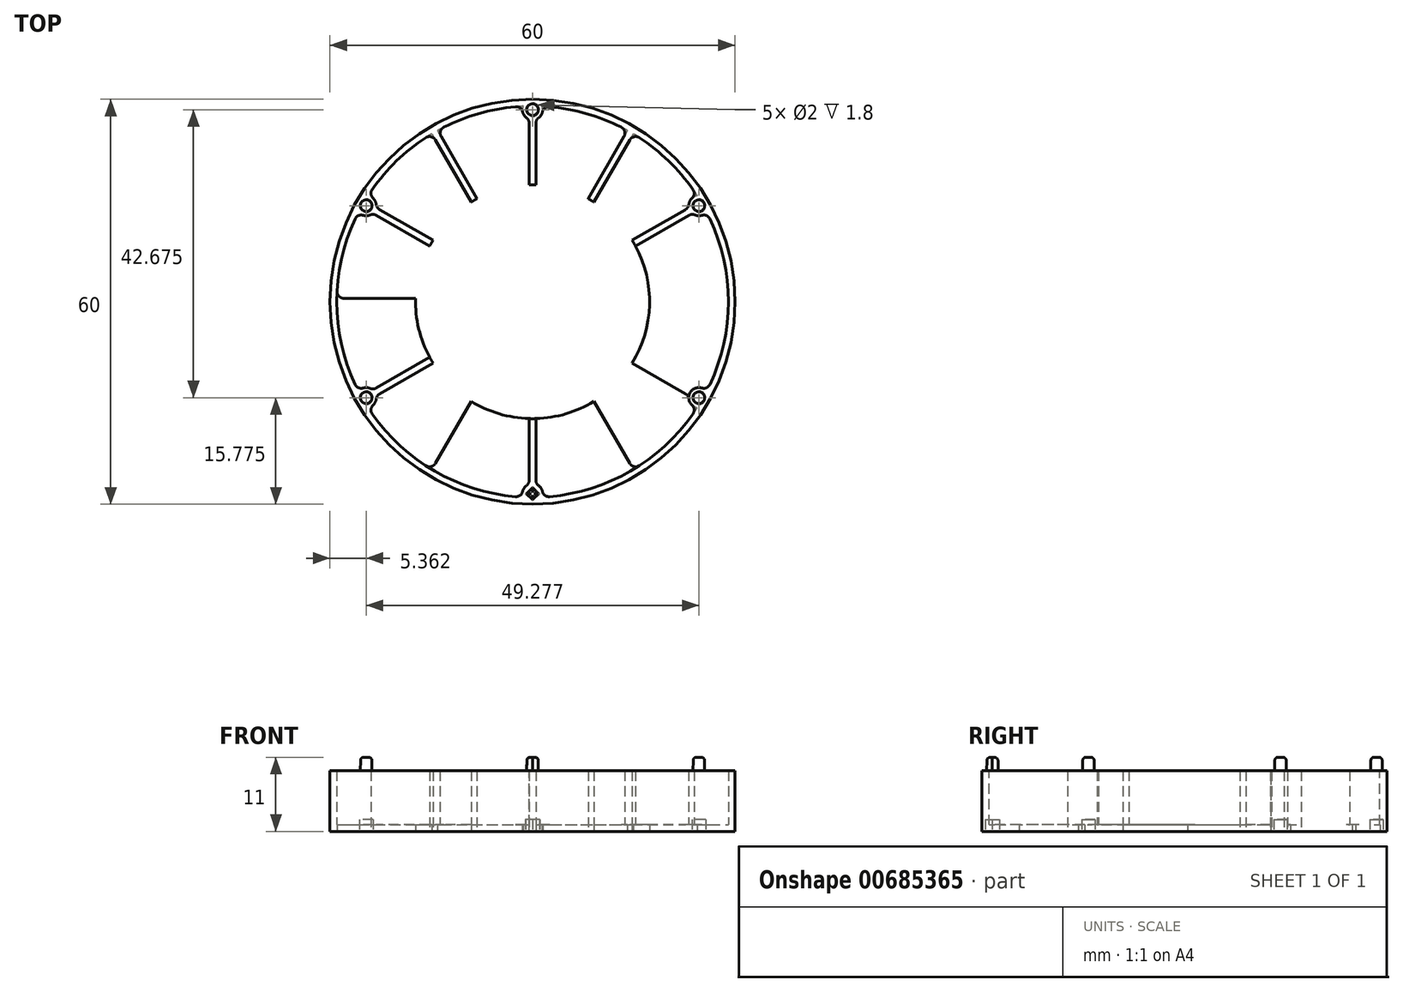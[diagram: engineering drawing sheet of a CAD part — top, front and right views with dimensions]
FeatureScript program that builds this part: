
annotation { "Feature Type Name" : "Feature", "Feature Type Description" : "" }
export const myFeature = defineFeature(function(context is Context, id is Id, definition is map)
    precondition{}
    {
        {
            var Q0;
            Q0=qCreatedBy(makeId("Top.planeOp"),FACE);
            var sketch = newSketch(context, id + "F0", { "sketchPlane" : qUnion([Q0])});
            skCircle(sketch, "E0", {"center": v(0, 0) * mm, "radius": 30 * mm});
            skCircle(sketch, "E1.0", {"center": v(0, 0) * mm, "radius": 29 * mm});
            skLineSegment(sketch, "E2.bottom", {"start": v(14.56, 26.23) * mm, "end": v(15.43, 25.73) * mm});
            skLineSegment(sketch, "E2.top", {"start": v(-15.43, -25.73) * mm, "end": v(-14.56, -26.23) * mm});
            skLineSegment(sketch, "E2.left", {"start": v(14.56, 26.23) * mm, "end": v(-15.43, -25.73) * mm});
            skLineSegment(sketch, "E2.right", {"start": v(15.43, 25.73) * mm, "end": v(-14.56, -26.23) * mm});
            skLineSegment(sketch, "E3.bottom", {"start": v(25.73, 15.43) * mm, "end": v(26.23, 14.56) * mm});
            skLineSegment(sketch, "E3.top", {"start": v(-26.23, -14.56) * mm, "end": v(-25.73, -15.43) * mm});
            skLineSegment(sketch, "E3.left", {"start": v(25.73, 15.43) * mm, "end": v(-26.23, -14.56) * mm});
            skLineSegment(sketch, "E3.right", {"start": v(26.23, 14.56) * mm, "end": v(-25.73, -15.43) * mm});
            skLineSegment(sketch, "E4", {"start": v(-38.35, 0) * mm, "end": v(39.17, 0) * mm, "construction": true});
            skLineSegment(sketch, "E5", {"start": v(0, 42.5) * mm, "end": v(0, -42.47) * mm, "construction": true});
            skLineSegment(sketch, "E6.bottom", {"start": v(-30, 0.5) * mm, "end": v(30, 0.5) * mm});
            skLineSegment(sketch, "E6.top", {"start": v(-30, -0.5) * mm, "end": v(30, -0.5) * mm});
            skLineSegment(sketch, "E6.left", {"start": v(-30, 0.5) * mm, "end": v(-30, -0.5) * mm});
            skLineSegment(sketch, "E6.right", {"start": v(30, 0.5) * mm, "end": v(30, -0.5) * mm});
            skLineSegment(sketch, "E7.bottom", {"start": v(-25.73, 15.43) * mm, "end": v(26.23, -14.56) * mm});
            skLineSegment(sketch, "E7.top", {"start": v(-26.23, 14.56) * mm, "end": v(25.73, -15.43) * mm});
            skLineSegment(sketch, "E7.left", {"start": v(-25.73, 15.43) * mm, "end": v(-26.23, 14.56) * mm});
            skLineSegment(sketch, "E7.right", {"start": v(26.23, -14.56) * mm, "end": v(25.73, -15.43) * mm});
            skLineSegment(sketch, "E8.bottom", {"start": v(-0.5, 30) * mm, "end": v(0.5, 30) * mm});
            skLineSegment(sketch, "E8.top", {"start": v(-0.5, -30) * mm, "end": v(0.5, -30) * mm});
            skLineSegment(sketch, "E8.left", {"start": v(-0.5, 30) * mm, "end": v(-0.5, -30) * mm});
            skLineSegment(sketch, "E8.right", {"start": v(0.5, 30) * mm, "end": v(0.5, -30) * mm});
            skLineSegment(sketch, "E9.bottom", {"start": v(-15.43, 25.73) * mm, "end": v(-14.56, 26.23) * mm});
            skLineSegment(sketch, "E9.top", {"start": v(14.56, -26.23) * mm, "end": v(15.43, -25.73) * mm});
            skLineSegment(sketch, "E9.left", {"start": v(-15.43, 25.73) * mm, "end": v(14.56, -26.23) * mm});
            skLineSegment(sketch, "E9.right", {"start": v(-14.56, 26.23) * mm, "end": v(15.43, -25.73) * mm});
            skCircle(sketch, "E10", {"center": v(0, 0) * mm, "radius": 17.33 * mm});
            skSolve(sketch);
        }
        {
            var Q0;
            Q0=qCreatedBy(makeId("Top.planeOp"),FACE);
            var sketch = newSketch(context, id + "F1", { "sketchPlane" : qUnion([Q0])});
            skCircle(sketch, "E11", {"center": v(0, 0) * mm, "radius": 30 * mm});
            skCircle(sketch, "E12", {"center": v(0, 0) * mm, "radius": 29 * mm});
            skSolve(sketch);
        }
        {
            var Q0;
            Q0=makeQuery(id+"F1.imprint","IMPRINT",FACE,{"disambiguationData":[TD([[makeQuery(id+"F1.imprint","IMPRINT",EDGE,{"derivedFrom":sQuery(id+"F1.wireOp",EDGE,"E11")}),1.0]])]});
            extrude(context, id + "F2", {"entities" : qUnion([Q0]), "depth" : 9 * mm, "offsetDistance" : 25 * mm});
        }
        {
            var Q0;
            {var subQ0=sQuery(id+"F0.wireOp",EDGE,"E7.bottom");var subQ1=sQuery(id+"F0.wireOp",EDGE,"E1.0");var subQ2=makeQuery(id+"F0.imprint","INTERSECT",VERTEX,{"disambiguationData":[OD(0.0)],"derivedFrom":[subQ1,subQ0]});Q0=makeQuery(id+"F0.imprint","IMPRINT",FACE,{"disambiguationData":[TD([[makeQuery(id+"F0.imprint","IMPRINT",EDGE,{"disambiguationData":[TD([[subQ2,-1.0]])],"derivedFrom":subQ1}),1.0]])]});}
            var Q1;
            {var subQ0=sQuery(id+"F0.wireOp",EDGE,"E2.right");var subQ1=sQuery(id+"F0.wireOp",EDGE,"E1.0");var subQ2=makeQuery(id+"F0.imprint","INTERSECT",VERTEX,{"disambiguationData":[OD(0.0)],"derivedFrom":[subQ1,subQ0]});Q1=makeQuery(id+"F0.imprint","IMPRINT",FACE,{"disambiguationData":[TD([[makeQuery(id+"F0.imprint","IMPRINT",EDGE,{"disambiguationData":[TD([[subQ2,-1.0]])],"derivedFrom":subQ1}),1.0]])]});}
            var Q2;
            {var subQ0=sQuery(id+"F0.wireOp",EDGE,"E8.left");var subQ1=sQuery(id+"F0.wireOp",EDGE,"E1.0");var subQ2=makeQuery(id+"F0.imprint","INTERSECT",VERTEX,{"disambiguationData":[OD(1.0)],"derivedFrom":[subQ1,subQ0]});Q2=makeQuery(id+"F0.imprint","IMPRINT",FACE,{"disambiguationData":[TD([[makeQuery(id+"F0.imprint","IMPRINT",EDGE,{"disambiguationData":[TD([[subQ2,-1.0]])],"derivedFrom":subQ1}),1.0]])]});}
            var Q3;
            {var subQ0=sQuery(id+"F0.wireOp",EDGE,"E3.left");var subQ1=sQuery(id+"F0.wireOp",EDGE,"E1.0");var subQ2=makeQuery(id+"F0.imprint","INTERSECT",VERTEX,{"disambiguationData":[OD(1.0)],"derivedFrom":[subQ1,subQ0]});Q3=makeQuery(id+"F0.imprint","IMPRINT",FACE,{"disambiguationData":[TD([[makeQuery(id+"F0.imprint","IMPRINT",EDGE,{"disambiguationData":[TD([[subQ2,-1.0]])],"derivedFrom":subQ1}),1.0]])]});}
            var Q4;
            {var subQ0=sQuery(id+"F0.wireOp",EDGE,"E9.right");var subQ1=sQuery(id+"F0.wireOp",EDGE,"E1.0");var subQ2=makeQuery(id+"F0.imprint","INTERSECT",VERTEX,{"disambiguationData":[OD(0.0)],"derivedFrom":[subQ1,subQ0]});Q4=makeQuery(id+"F0.imprint","IMPRINT",FACE,{"disambiguationData":[TD([[makeQuery(id+"F0.imprint","IMPRINT",EDGE,{"disambiguationData":[TD([[subQ2,-1.0]])],"derivedFrom":subQ1}),1.0]])]});}
            var Q5;
            {var subQ0=sQuery(id+"F0.wireOp",EDGE,"E8.right");var subQ1=sQuery(id+"F0.wireOp",EDGE,"E1.0");var subQ2=makeQuery(id+"F0.imprint","INTERSECT",VERTEX,{"disambiguationData":[OD(0.0)],"derivedFrom":[subQ1,subQ0]});Q5=makeQuery(id+"F0.imprint","IMPRINT",FACE,{"disambiguationData":[TD([[makeQuery(id+"F0.imprint","IMPRINT",EDGE,{"disambiguationData":[TD([[subQ2,-1.0]])],"derivedFrom":subQ1}),1.0]])]});}
            var Q6;
            {var subQ0=sQuery(id+"F0.wireOp",EDGE,"E3.right");var subQ1=sQuery(id+"F0.wireOp",EDGE,"E1.0");var subQ2=makeQuery(id+"F0.imprint","INTERSECT",VERTEX,{"disambiguationData":[OD(0.0)],"derivedFrom":[subQ1,subQ0]});Q6=makeQuery(id+"F0.imprint","IMPRINT",FACE,{"disambiguationData":[TD([[makeQuery(id+"F0.imprint","IMPRINT",EDGE,{"disambiguationData":[TD([[subQ2,-1.0]])],"derivedFrom":subQ1}),1.0]])]});}
            extrude(context, id + "F3", {"entities" : qUnion([Q0, Q1, Q2, Q3, Q4, Q5, Q6]), "operationType" : NewBodyOperationType.ADD, "depth" : 9 * mm, "offsetDistance" : 25 * mm});
        }
        {
            var Q0;
            Q0=makeQuery(id+"F1.imprint","IMPRINT",FACE,{"disambiguationData":[TD([[makeQuery(id+"F1.imprint","IMPRINT",EDGE,{"derivedFrom":sQuery(id+"F1.wireOp",EDGE,"E11")}),1.0]])]});
            var Q1;
            Q1=makeQuery(id+"F1.imprint","IMPRINT",FACE,{"disambiguationData":[TD([[makeQuery(id+"F1.imprint","IMPRINT",EDGE,{"derivedFrom":sQuery(id+"F1.wireOp",EDGE,"E12")}),1.0]])]});
            extrude(context, id + "F4", {"entities" : qUnion([Q0, Q1]), "operationType" : NewBodyOperationType.ADD, "depth" : 1 * mm, "offsetDistance" : 25 * mm});
        }
        {
            var Q0;
            {var subQ0=sQuery(id+"F0.wireOp",EDGE,"E9.right");var subQ1=sQuery(id+"F0.wireOp",EDGE,"E1.0");var subQ2=makeQuery(id+"F0.imprint","INTERSECT",VERTEX,{"disambiguationData":[OD(1.0)],"derivedFrom":[subQ1,subQ0]});Q0=makeQuery(id+"F0.imprint","IMPRINT",FACE,{"disambiguationData":[TD([[makeQuery(id+"F0.imprint","IMPRINT",EDGE,{"disambiguationData":[TD([[subQ2,-1.0]])],"derivedFrom":subQ1}),1.0]])]});}
            var Q1;
            {var subQ0=sQuery(id+"F0.wireOp",EDGE,"E3.left");var subQ1=sQuery(id+"F0.wireOp",EDGE,"E1.0");var subQ2=makeQuery(id+"F0.imprint","INTERSECT",VERTEX,{"disambiguationData":[OD(0.0)],"derivedFrom":[subQ1,subQ0]});Q1=makeQuery(id+"F0.imprint","IMPRINT",FACE,{"disambiguationData":[TD([[makeQuery(id+"F0.imprint","IMPRINT",EDGE,{"disambiguationData":[TD([[subQ2,-1.0]])],"derivedFrom":subQ1}),1.0]])]});}
            var Q2;
            {var subQ0=sQuery(id+"F0.wireOp",EDGE,"E2.left");var subQ1=sQuery(id+"F0.wireOp",EDGE,"E1.0");var subQ2=makeQuery(id+"F0.imprint","INTERSECT",VERTEX,{"disambiguationData":[OD(0.0)],"derivedFrom":[subQ1,subQ0]});Q2=makeQuery(id+"F0.imprint","IMPRINT",FACE,{"disambiguationData":[TD([[makeQuery(id+"F0.imprint","IMPRINT",EDGE,{"disambiguationData":[TD([[subQ2,-1.0]])],"derivedFrom":subQ1}),1.0]])]});}
            var Q3;
            {var subQ0=sQuery(id+"F0.wireOp",EDGE,"E8.left");var subQ1=sQuery(id+"F0.wireOp",EDGE,"E1.0");var subQ2=makeQuery(id+"F0.imprint","INTERSECT",VERTEX,{"disambiguationData":[OD(0.0)],"derivedFrom":[subQ1,subQ0]});Q3=makeQuery(id+"F0.imprint","IMPRINT",FACE,{"disambiguationData":[TD([[makeQuery(id+"F0.imprint","IMPRINT",EDGE,{"disambiguationData":[TD([[subQ2,-1.0]])],"derivedFrom":subQ1}),1.0]])]});}
            var Q4;
            {var subQ0=sQuery(id+"F0.wireOp",EDGE,"E9.left");var subQ1=sQuery(id+"F0.wireOp",EDGE,"E1.0");var subQ2=makeQuery(id+"F0.imprint","INTERSECT",VERTEX,{"disambiguationData":[OD(0.0)],"derivedFrom":[subQ1,subQ0]});Q4=makeQuery(id+"F0.imprint","IMPRINT",FACE,{"disambiguationData":[TD([[makeQuery(id+"F0.imprint","IMPRINT",EDGE,{"disambiguationData":[TD([[subQ2,-1.0]])],"derivedFrom":subQ1}),1.0]])]});}
            var Q5;
            {var subQ0=sQuery(id+"F0.wireOp",EDGE,"E7.top");var subQ1=sQuery(id+"F0.wireOp",EDGE,"E1.0");var subQ2=makeQuery(id+"F0.imprint","INTERSECT",VERTEX,{"disambiguationData":[OD(0.0)],"derivedFrom":[subQ1,subQ0]});Q5=makeQuery(id+"F0.imprint","IMPRINT",FACE,{"disambiguationData":[TD([[makeQuery(id+"F0.imprint","IMPRINT",EDGE,{"disambiguationData":[TD([[subQ2,-1.0]])],"derivedFrom":subQ1}),1.0]])]});}
            var Q6;
            {var subQ0=sQuery(id+"F0.wireOp",EDGE,"E3.right");var subQ1=sQuery(id+"F0.wireOp",EDGE,"E1.0");var subQ2=makeQuery(id+"F0.imprint","INTERSECT",VERTEX,{"disambiguationData":[OD(1.0)],"derivedFrom":[subQ1,subQ0]});Q6=makeQuery(id+"F0.imprint","IMPRINT",FACE,{"disambiguationData":[TD([[makeQuery(id+"F0.imprint","IMPRINT",EDGE,{"disambiguationData":[TD([[subQ2,-1.0]])],"derivedFrom":subQ1}),1.0]])]});}
            extrude(context, id + "F5", {"entities" : qUnion([Q0, Q1, Q2, Q3, Q4, Q5, Q6]), "operationType" : NewBodyOperationType.REMOVE, "depth" : 1 * mm, "offsetDistance" : 25 * mm});
        }
        {
            var Q0;
            Q0=qCreatedBy(makeId("Top.planeOp"),FACE);
            var sketch = newSketch(context, id + "F6", { "sketchPlane" : qUnion([Q0])});
            skCircle(sketch, "E13", {"center": v(0, 0) * mm, "radius": 28.45 * mm});
            skLineSegment(sketch, "E14", {"start": v(0, 28.45) * mm, "end": v(0, -28.45) * mm, "construction": true});
            skLineSegment(sketch, "E15", {"start": v(24.64, 14.22) * mm, "end": v(0, 0) * mm, "construction": true});
            skLineSegment(sketch, "E16", {"start": v(14.23, 24.64) * mm, "end": v(0, 0) * mm, "construction": true});
            skLineSegment(sketch, "E17", {"start": v(0, 0) * mm, "end": v(28.45, 0) * mm, "construction": true});
            skLineSegment(sketch, "E18", {"start": v(0, 0) * mm, "end": v(24.64, -14.22) * mm, "construction": true});
            skLineSegment(sketch, "E19", {"start": v(0, 0) * mm, "end": v(14.23, -24.64) * mm, "construction": true});
            skLineSegment(sketch, "E20", {"start": v(0, 0) * mm, "end": v(-14.23, 24.64) * mm, "construction": true});
            skLineSegment(sketch, "E21", {"start": v(0, 0) * mm, "end": v(-24.64, 14.22) * mm, "construction": true});
            skLineSegment(sketch, "E22", {"start": v(0, 0) * mm, "end": v(-28.45, 0) * mm, "construction": true});
            skLineSegment(sketch, "E23", {"start": v(0, 0) * mm, "end": v(-24.64, -14.23) * mm, "construction": true});
            skLineSegment(sketch, "E24", {"start": v(0, 0) * mm, "end": v(-14.22, -24.64) * mm, "construction": true});
            skCircle(sketch, "E25", {"center": v(0, 28.45) * mm, "radius": 1.5 * mm});
            skCircle(sketch, "E26", {"center": v(24.64, 14.22) * mm, "radius": 1.5 * mm});
            skCircle(sketch, "E27", {"center": v(24.64, -14.22) * mm, "radius": 1.5 * mm});
            skCircle(sketch, "E28", {"center": v(0, -28.45) * mm, "radius": 1.5 * mm});
            skCircle(sketch, "E29", {"center": v(-24.64, -14.23) * mm, "radius": 1.5 * mm});
            skCircle(sketch, "E30", {"center": v(-24.64, 14.22) * mm, "radius": 1.5 * mm});
            skCircle(sketch, "E31", {"center": v(-24.64, 14.22) * mm, "radius": 1 * mm});
            skCircle(sketch, "E32", {"center": v(0, 28.45) * mm, "radius": 1 * mm});
            skCircle(sketch, "E33", {"center": v(24.64, 14.22) * mm, "radius": 1 * mm});
            skCircle(sketch, "E34", {"center": v(24.64, -14.22) * mm, "radius": 1 * mm});
            skCircle(sketch, "E35", {"center": v(-24.64, -14.23) * mm, "radius": 1 * mm});
            skLineSegment(sketch, "E36.bottom", {"start": v(1.06, -28.45) * mm, "end": v(0, -29.51) * mm});
            skLineSegment(sketch, "E36.top", {"start": v(0, -27.39) * mm, "end": v(-1.06, -28.45) * mm});
            skLineSegment(sketch, "E36.left", {"start": v(1.06, -28.45) * mm, "end": v(0, -27.39) * mm});
            skLineSegment(sketch, "E36.right", {"start": v(0, -29.51) * mm, "end": v(-1.06, -28.45) * mm});
            skSolve(sketch);
        }
        {
            var Q0;
            {var subQ0=sQuery(id+"F6.wireOp",EDGE,"E30");var subQ1=sQuery(id+"F6.wireOp",EDGE,"E13");var subQ2=makeQuery(id+"F6.imprint","INTERSECT",VERTEX,{"disambiguationData":[OD(0.0)],"derivedFrom":[subQ1,subQ0]});Q0=makeQuery(id+"F6.imprint","IMPRINT",FACE,{"disambiguationData":[TD([[makeQuery(id+"F6.imprint","IMPRINT",EDGE,{"disambiguationData":[TD([[subQ2,-1.0]])],"derivedFrom":subQ1}),1.0]])]});}
            var Q1;
            {var subQ0=sQuery(id+"F6.wireOp",EDGE,"E30");var subQ1=sQuery(id+"F6.wireOp",EDGE,"E13");var subQ2=makeQuery(id+"F6.imprint","INTERSECT",VERTEX,{"disambiguationData":[OD(0.0)],"derivedFrom":[subQ1,subQ0]});Q1=makeQuery(id+"F6.imprint","IMPRINT",FACE,{"disambiguationData":[TD([[makeQuery(id+"F6.imprint","IMPRINT",EDGE,{"disambiguationData":[TD([[subQ2,-1.0]])],"derivedFrom":subQ1}),-1.0]])]});}
            var Q2;
            {var subQ0=sQuery(id+"F6.wireOp",EDGE,"E25");var subQ1=sQuery(id+"F6.wireOp",EDGE,"E13");var subQ2=makeQuery(id+"F6.imprint","INTERSECT",VERTEX,{"disambiguationData":[OD(0.0)],"derivedFrom":[subQ1,subQ0]});Q2=makeQuery(id+"F6.imprint","IMPRINT",FACE,{"disambiguationData":[TD([[makeQuery(id+"F6.imprint","IMPRINT",EDGE,{"disambiguationData":[TD([[subQ2,-1.0]])],"derivedFrom":subQ1}),1.0]])]});}
            var Q3;
            {var subQ0=sQuery(id+"F6.wireOp",EDGE,"E25");var subQ1=sQuery(id+"F6.wireOp",EDGE,"E13");var subQ2=makeQuery(id+"F6.imprint","INTERSECT",VERTEX,{"disambiguationData":[OD(0.0)],"derivedFrom":[subQ1,subQ0]});Q3=makeQuery(id+"F6.imprint","IMPRINT",FACE,{"disambiguationData":[TD([[makeQuery(id+"F6.imprint","IMPRINT",EDGE,{"disambiguationData":[TD([[subQ2,-1.0]])],"derivedFrom":subQ1}),-1.0]])]});}
            var Q4;
            {var subQ0=sQuery(id+"F6.wireOp",EDGE,"E26");var subQ1=sQuery(id+"F6.wireOp",EDGE,"E13");var subQ2=makeQuery(id+"F6.imprint","INTERSECT",VERTEX,{"disambiguationData":[OD(0.0)],"derivedFrom":[subQ1,subQ0]});Q4=makeQuery(id+"F6.imprint","IMPRINT",FACE,{"disambiguationData":[TD([[makeQuery(id+"F6.imprint","IMPRINT",EDGE,{"disambiguationData":[TD([[subQ2,-1.0]])],"derivedFrom":subQ1}),-1.0]])]});}
            var Q5;
            {var subQ0=sQuery(id+"F6.wireOp",EDGE,"E26");var subQ1=sQuery(id+"F6.wireOp",EDGE,"E13");var subQ2=makeQuery(id+"F6.imprint","INTERSECT",VERTEX,{"disambiguationData":[OD(0.0)],"derivedFrom":[subQ1,subQ0]});Q5=makeQuery(id+"F6.imprint","IMPRINT",FACE,{"disambiguationData":[TD([[makeQuery(id+"F6.imprint","IMPRINT",EDGE,{"disambiguationData":[TD([[subQ2,-1.0]])],"derivedFrom":subQ1}),1.0]])]});}
            var Q6;
            {var subQ0=sQuery(id+"F6.wireOp",EDGE,"E29");var subQ1=sQuery(id+"F6.wireOp",EDGE,"E13");var subQ2=makeQuery(id+"F6.imprint","INTERSECT",VERTEX,{"disambiguationData":[OD(0.0)],"derivedFrom":[subQ1,subQ0]});Q6=makeQuery(id+"F6.imprint","IMPRINT",FACE,{"disambiguationData":[TD([[makeQuery(id+"F6.imprint","IMPRINT",EDGE,{"disambiguationData":[TD([[subQ2,-1.0]])],"derivedFrom":subQ1}),1.0]])]});}
            var Q7;
            {var subQ0=sQuery(id+"F6.wireOp",EDGE,"E29");var subQ1=sQuery(id+"F6.wireOp",EDGE,"E13");var subQ2=makeQuery(id+"F6.imprint","INTERSECT",VERTEX,{"disambiguationData":[OD(0.0)],"derivedFrom":[subQ1,subQ0]});Q7=makeQuery(id+"F6.imprint","IMPRINT",FACE,{"disambiguationData":[TD([[makeQuery(id+"F6.imprint","IMPRINT",EDGE,{"disambiguationData":[TD([[subQ2,-1.0]])],"derivedFrom":subQ1}),-1.0]])]});}
            var Q8;
            {var subQ3=sQuery(id+"F6.wireOp",EDGE,"E13");var subQ5=sQuery(id+"F6.wireOp",EDGE,"E28");var subQ6=makeQuery(id+"F6.imprint","INTERSECT",VERTEX,{"disambiguationData":[OD(0.0)],"derivedFrom":[subQ3,subQ5]});Q8=makeQuery(id+"F6.imprint","IMPRINT",FACE,{"disambiguationData":[TD([[makeQuery(id+"F6.imprint","IMPRINT",EDGE,{"disambiguationData":[TD([[subQ6,-1.0]])],"derivedFrom":subQ3}),1.0]])]});}
            var Q9;
            {var subQ6=sQuery(id+"F6.wireOp",EDGE,"E36.bottom");Q9=makeQuery(id+"F6.imprint","IMPRINT",FACE,{"disambiguationData":[TD([[makeQuery(id+"F6.imprint","IMPRINT",EDGE,{"derivedFrom":subQ6}),1.0]])]});}
            var Q10;
            {var subQ0=sQuery(id+"F6.wireOp",EDGE,"E27");var subQ1=sQuery(id+"F6.wireOp",EDGE,"E13");var subQ2=makeQuery(id+"F6.imprint","INTERSECT",VERTEX,{"disambiguationData":[OD(0.0)],"derivedFrom":[subQ1,subQ0]});Q10=makeQuery(id+"F6.imprint","IMPRINT",FACE,{"disambiguationData":[TD([[makeQuery(id+"F6.imprint","IMPRINT",EDGE,{"disambiguationData":[TD([[subQ2,-1.0]])],"derivedFrom":subQ1}),-1.0]])]});}
            var Q11;
            {var subQ0=sQuery(id+"F6.wireOp",EDGE,"E27");var subQ1=sQuery(id+"F6.wireOp",EDGE,"E13");var subQ2=makeQuery(id+"F6.imprint","INTERSECT",VERTEX,{"disambiguationData":[OD(0.0)],"derivedFrom":[subQ1,subQ0]});Q11=makeQuery(id+"F6.imprint","IMPRINT",FACE,{"disambiguationData":[TD([[makeQuery(id+"F6.imprint","IMPRINT",EDGE,{"disambiguationData":[TD([[subQ2,-1.0]])],"derivedFrom":subQ1}),1.0]])]});}
            var Q12;
            {var subQ0=sQuery(id+"F6.wireOp",EDGE,"E31");var subQ1=sQuery(id+"F6.wireOp",EDGE,"E13");var subQ2=makeQuery(id+"F6.imprint","INTERSECT",VERTEX,{"disambiguationData":[OD(0.0)],"derivedFrom":[subQ1,subQ0]});Q12=makeQuery(id+"F6.imprint","IMPRINT",FACE,{"disambiguationData":[TD([[makeQuery(id+"F6.imprint","IMPRINT",EDGE,{"disambiguationData":[TD([[subQ2,-1.0]])],"derivedFrom":subQ1}),1.0]])]});}
            var Q13;
            {var subQ0=sQuery(id+"F6.wireOp",EDGE,"E31");var subQ1=sQuery(id+"F6.wireOp",EDGE,"E13");var subQ2=makeQuery(id+"F6.imprint","INTERSECT",VERTEX,{"disambiguationData":[OD(0.0)],"derivedFrom":[subQ1,subQ0]});Q13=makeQuery(id+"F6.imprint","IMPRINT",FACE,{"disambiguationData":[TD([[makeQuery(id+"F6.imprint","IMPRINT",EDGE,{"disambiguationData":[TD([[subQ2,-1.0]])],"derivedFrom":subQ1}),-1.0]])]});}
            var Q14;
            {var subQ0=sQuery(id+"F6.wireOp",EDGE,"E32");var subQ1=sQuery(id+"F6.wireOp",EDGE,"E13");var subQ2=makeQuery(id+"F6.imprint","INTERSECT",VERTEX,{"disambiguationData":[OD(0.0)],"derivedFrom":[subQ1,subQ0]});Q14=makeQuery(id+"F6.imprint","IMPRINT",FACE,{"disambiguationData":[TD([[makeQuery(id+"F6.imprint","IMPRINT",EDGE,{"disambiguationData":[TD([[subQ2,-1.0]])],"derivedFrom":subQ1}),-1.0]])]});}
            var Q15;
            {var subQ0=sQuery(id+"F6.wireOp",EDGE,"E32");var subQ1=sQuery(id+"F6.wireOp",EDGE,"E13");var subQ2=makeQuery(id+"F6.imprint","INTERSECT",VERTEX,{"disambiguationData":[OD(0.0)],"derivedFrom":[subQ1,subQ0]});Q15=makeQuery(id+"F6.imprint","IMPRINT",FACE,{"disambiguationData":[TD([[makeQuery(id+"F6.imprint","IMPRINT",EDGE,{"disambiguationData":[TD([[subQ2,-1.0]])],"derivedFrom":subQ1}),1.0]])]});}
            var Q16;
            {var subQ0=sQuery(id+"F6.wireOp",EDGE,"E33");var subQ1=sQuery(id+"F6.wireOp",EDGE,"E13");var subQ2=makeQuery(id+"F6.imprint","INTERSECT",VERTEX,{"disambiguationData":[OD(0.0)],"derivedFrom":[subQ1,subQ0]});Q16=makeQuery(id+"F6.imprint","IMPRINT",FACE,{"disambiguationData":[TD([[makeQuery(id+"F6.imprint","IMPRINT",EDGE,{"disambiguationData":[TD([[subQ2,-1.0]])],"derivedFrom":subQ1}),-1.0]])]});}
            var Q17;
            {var subQ0=sQuery(id+"F6.wireOp",EDGE,"E33");var subQ1=sQuery(id+"F6.wireOp",EDGE,"E13");var subQ2=makeQuery(id+"F6.imprint","INTERSECT",VERTEX,{"disambiguationData":[OD(0.0)],"derivedFrom":[subQ1,subQ0]});Q17=makeQuery(id+"F6.imprint","IMPRINT",FACE,{"disambiguationData":[TD([[makeQuery(id+"F6.imprint","IMPRINT",EDGE,{"disambiguationData":[TD([[subQ2,-1.0]])],"derivedFrom":subQ1}),1.0]])]});}
            var Q18;
            {var subQ0=sQuery(id+"F6.wireOp",EDGE,"E34");var subQ1=sQuery(id+"F6.wireOp",EDGE,"E13");var subQ2=makeQuery(id+"F6.imprint","INTERSECT",VERTEX,{"disambiguationData":[OD(0.0)],"derivedFrom":[subQ1,subQ0]});Q18=makeQuery(id+"F6.imprint","IMPRINT",FACE,{"disambiguationData":[TD([[makeQuery(id+"F6.imprint","IMPRINT",EDGE,{"disambiguationData":[TD([[subQ2,-1.0]])],"derivedFrom":subQ1}),-1.0]])]});}
            var Q19;
            {var subQ0=sQuery(id+"F6.wireOp",EDGE,"E34");var subQ1=sQuery(id+"F6.wireOp",EDGE,"E13");var subQ2=makeQuery(id+"F6.imprint","INTERSECT",VERTEX,{"disambiguationData":[OD(0.0)],"derivedFrom":[subQ1,subQ0]});Q19=makeQuery(id+"F6.imprint","IMPRINT",FACE,{"disambiguationData":[TD([[makeQuery(id+"F6.imprint","IMPRINT",EDGE,{"disambiguationData":[TD([[subQ2,-1.0]])],"derivedFrom":subQ1}),1.0]])]});}
            var Q20;
            {var subQ1=sQuery(id+"F6.wireOp",EDGE,"E36.bottom");Q20=makeQuery(id+"F6.imprint","IMPRINT",FACE,{"disambiguationData":[TD([[makeQuery(id+"F6.imprint","IMPRINT",EDGE,{"derivedFrom":subQ1}),-1.0]])]});}
            var Q21;
            {var subQ0=sQuery(id+"F6.wireOp",EDGE,"E35");var subQ1=sQuery(id+"F6.wireOp",EDGE,"E13");var subQ2=makeQuery(id+"F6.imprint","INTERSECT",VERTEX,{"disambiguationData":[OD(0.0)],"derivedFrom":[subQ1,subQ0]});Q21=makeQuery(id+"F6.imprint","IMPRINT",FACE,{"disambiguationData":[TD([[makeQuery(id+"F6.imprint","IMPRINT",EDGE,{"disambiguationData":[TD([[subQ2,-1.0]])],"derivedFrom":subQ1}),-1.0]])]});}
            var Q22;
            {var subQ0=sQuery(id+"F6.wireOp",EDGE,"E35");var subQ1=sQuery(id+"F6.wireOp",EDGE,"E13");var subQ2=makeQuery(id+"F6.imprint","INTERSECT",VERTEX,{"disambiguationData":[OD(0.0)],"derivedFrom":[subQ1,subQ0]});Q22=makeQuery(id+"F6.imprint","IMPRINT",FACE,{"disambiguationData":[TD([[makeQuery(id+"F6.imprint","IMPRINT",EDGE,{"disambiguationData":[TD([[subQ2,-1.0]])],"derivedFrom":subQ1}),1.0]])]});}
            var Q23;
            {var subQ0=sQuery(id+"F6.wireOp",EDGE,"E36.top");var subQ1=sQuery(id+"F6.wireOp",EDGE,"E13");var subQ2=makeQuery(id+"F6.imprint","INTERSECT",VERTEX,{"derivedFrom":[subQ1,subQ0]});Q23=makeQuery(id+"F6.imprint","IMPRINT",FACE,{"disambiguationData":[TD([[makeQuery(id+"F6.imprint","IMPRINT",EDGE,{"disambiguationData":[TD([[subQ2,-1.0]])],"derivedFrom":subQ1}),1.0]])]});}
            extrude(context, id + "F7", {"entities" : qUnion([Q0, Q1, Q2, Q3, Q4, Q5, Q6, Q7, Q8, Q9, Q10, Q11, Q12, Q13, Q14, Q15, Q16, Q17, Q18, Q19, Q20, Q21, Q22, Q23]), "operationType" : NewBodyOperationType.ADD, "depth" : 9 * mm, "offsetDistance" : 25 * mm});
        }
        {
            var Q0;
            {var subQ0=sQuery(id+"F0.wireOp",EDGE,"E8.right");var subQ1=sQuery(id+"F0.wireOp",EDGE,"E1.0");Q0=makeQuery(id+"F3.opExtrude","SWEPT_EDGE",EDGE,{"disambiguationData":[OSD([subQ1,subQ0]),TDD([makeQuery(id+"F0.imprint","INTERSECT",VERTEX,{"disambiguationData":[OD(1.0)],"derivedFrom":[subQ1,subQ0]})])]});}
            var Q1;
            {var subQ0=sQuery(id+"F0.wireOp",EDGE,"E2.left");var subQ1=sQuery(id+"F0.wireOp",EDGE,"E1.0");Q1=makeQuery(id+"F3.opExtrude","SWEPT_EDGE",EDGE,{"disambiguationData":[OSD([subQ1,subQ0]),TDD([makeQuery(id+"F0.imprint","INTERSECT",VERTEX,{"disambiguationData":[OD(1.0)],"derivedFrom":[subQ1,subQ0]})])]});}
            var Q2;
            {var subQ0=sQuery(id+"F0.wireOp",EDGE,"E3.left");var subQ1=sQuery(id+"F0.wireOp",EDGE,"E1.0");Q2=makeQuery(id+"F3.opExtrude","SWEPT_EDGE",EDGE,{"disambiguationData":[OSD([subQ1,subQ0]),TDD([makeQuery(id+"F0.imprint","INTERSECT",VERTEX,{"disambiguationData":[OD(1.0)],"derivedFrom":[subQ1,subQ0]})])]});}
            var Q3;
            {var subQ0=sQuery(id+"F0.wireOp",EDGE,"E6.bottom");var subQ1=sQuery(id+"F0.wireOp",EDGE,"E1.0");Q3=makeQuery(id+"F3.opExtrude","SWEPT_EDGE",EDGE,{"disambiguationData":[OSD([subQ1,subQ0]),TDD([makeQuery(id+"F0.imprint","INTERSECT",VERTEX,{"disambiguationData":[OD(1.0)],"derivedFrom":[subQ1,subQ0]})])]});}
            var Q4;
            {var subQ0=sQuery(id+"F0.wireOp",EDGE,"E9.right");var subQ1=sQuery(id+"F0.wireOp",EDGE,"E1.0");Q4=makeQuery(id+"F3.opExtrude","SWEPT_EDGE",EDGE,{"disambiguationData":[OSD([subQ1,subQ0]),TDD([makeQuery(id+"F0.imprint","INTERSECT",VERTEX,{"disambiguationData":[OD(1.0)],"derivedFrom":[subQ1,subQ0]})])]});}
            var Q5;
            {var subQ0=sQuery(id+"F0.wireOp",EDGE,"E7.bottom");var subQ1=sQuery(id+"F0.wireOp",EDGE,"E1.0");Q5=makeQuery(id+"F3.opExtrude","SWEPT_EDGE",EDGE,{"disambiguationData":[OSD([subQ1,subQ0]),TDD([makeQuery(id+"F0.imprint","INTERSECT",VERTEX,{"disambiguationData":[OD(1.0)],"derivedFrom":[subQ1,subQ0]})])]});}
            var Q6;
            {var subQ0=sQuery(id+"F0.wireOp",EDGE,"E8.left");var subQ1=sQuery(id+"F0.wireOp",EDGE,"E1.0");Q6=makeQuery(id+"F3.opExtrude","SWEPT_EDGE",EDGE,{"disambiguationData":[OSD([subQ1,subQ0]),TDD([makeQuery(id+"F0.imprint","INTERSECT",VERTEX,{"disambiguationData":[OD(0.0)],"derivedFrom":[subQ1,subQ0]})])]});}
            var Q7;
            {var subQ0=sQuery(id+"F0.wireOp",EDGE,"E2.left");var subQ1=sQuery(id+"F0.wireOp",EDGE,"E1.0");Q7=makeQuery(id+"F3.opExtrude","SWEPT_EDGE",EDGE,{"disambiguationData":[OSD([subQ1,subQ0]),TDD([makeQuery(id+"F0.imprint","INTERSECT",VERTEX,{"disambiguationData":[OD(0.0)],"derivedFrom":[subQ1,subQ0]})])]});}
            var Q8;
            {var subQ0=sQuery(id+"F0.wireOp",EDGE,"E3.left");var subQ1=sQuery(id+"F0.wireOp",EDGE,"E1.0");Q8=makeQuery(id+"F3.opExtrude","SWEPT_EDGE",EDGE,{"disambiguationData":[OSD([subQ1,subQ0]),TDD([makeQuery(id+"F0.imprint","INTERSECT",VERTEX,{"disambiguationData":[OD(0.0)],"derivedFrom":[subQ1,subQ0]})])]});}
            var Q9;
            {var subQ0=sQuery(id+"F0.wireOp",EDGE,"E6.top");var subQ1=sQuery(id+"F0.wireOp",EDGE,"E1.0");Q9=makeQuery(id+"F3.opExtrude","SWEPT_EDGE",EDGE,{"disambiguationData":[OSD([subQ1,subQ0]),TDD([makeQuery(id+"F0.imprint","INTERSECT",VERTEX,{"disambiguationData":[OD(1.0)],"derivedFrom":[subQ1,subQ0]})])]});}
            var Q10;
            {var subQ0=sQuery(id+"F0.wireOp",EDGE,"E7.top");var subQ1=sQuery(id+"F0.wireOp",EDGE,"E1.0");Q10=makeQuery(id+"F3.opExtrude","SWEPT_EDGE",EDGE,{"disambiguationData":[OSD([subQ1,subQ0]),TDD([makeQuery(id+"F0.imprint","INTERSECT",VERTEX,{"disambiguationData":[OD(0.0)],"derivedFrom":[subQ1,subQ0]})])]});}
            var Q11;
            {var subQ0=sQuery(id+"F0.wireOp",EDGE,"E6.top");var subQ1=sQuery(id+"F0.wireOp",EDGE,"E1.0");Q11=makeQuery(id+"F3.opExtrude","SWEPT_EDGE",EDGE,{"disambiguationData":[OSD([subQ1,subQ0]),TDD([makeQuery(id+"F0.imprint","INTERSECT",VERTEX,{"disambiguationData":[OD(0.0)],"derivedFrom":[subQ1,subQ0]})])]});}
            var Q12;
            {var subQ0=sQuery(id+"F0.wireOp",EDGE,"E9.left");var subQ1=sQuery(id+"F0.wireOp",EDGE,"E1.0");Q12=makeQuery(id+"F3.opExtrude","SWEPT_EDGE",EDGE,{"disambiguationData":[OSD([subQ1,subQ0]),TDD([makeQuery(id+"F0.imprint","INTERSECT",VERTEX,{"disambiguationData":[OD(0.0)],"derivedFrom":[subQ1,subQ0]})])]});}
            var Q13;
            {var subQ0=sQuery(id+"F0.wireOp",EDGE,"E8.right");var subQ1=sQuery(id+"F0.wireOp",EDGE,"E1.0");Q13=makeQuery(id+"F3.opExtrude","SWEPT_EDGE",EDGE,{"disambiguationData":[OSD([subQ1,subQ0]),TDD([makeQuery(id+"F0.imprint","INTERSECT",VERTEX,{"disambiguationData":[OD(0.0)],"derivedFrom":[subQ1,subQ0]})])]});}
            var Q14;
            {var subQ0=sQuery(id+"F0.wireOp",EDGE,"E7.bottom");var subQ1=sQuery(id+"F0.wireOp",EDGE,"E1.0");Q14=makeQuery(id+"F3.opExtrude","SWEPT_EDGE",EDGE,{"disambiguationData":[OSD([subQ1,subQ0]),TDD([makeQuery(id+"F0.imprint","INTERSECT",VERTEX,{"disambiguationData":[OD(0.0)],"derivedFrom":[subQ1,subQ0]})])]});}
            var Q15;
            {var subQ0=sQuery(id+"F0.wireOp",EDGE,"E9.right");var subQ1=sQuery(id+"F0.wireOp",EDGE,"E1.0");Q15=makeQuery(id+"F3.opExtrude","SWEPT_EDGE",EDGE,{"disambiguationData":[OSD([subQ1,subQ0]),TDD([makeQuery(id+"F0.imprint","INTERSECT",VERTEX,{"disambiguationData":[OD(0.0)],"derivedFrom":[subQ1,subQ0]})])]});}
            var Q16;
            {var subQ0=sQuery(id+"F0.wireOp",EDGE,"E3.right");var subQ1=sQuery(id+"F0.wireOp",EDGE,"E1.0");Q16=makeQuery(id+"F3.opExtrude","SWEPT_EDGE",EDGE,{"disambiguationData":[OSD([subQ1,subQ0]),TDD([makeQuery(id+"F0.imprint","INTERSECT",VERTEX,{"disambiguationData":[OD(1.0)],"derivedFrom":[subQ1,subQ0]})])]});}
            var Q17;
            {var subQ0=sQuery(id+"F0.wireOp",EDGE,"E2.right");var subQ1=sQuery(id+"F0.wireOp",EDGE,"E1.0");Q17=makeQuery(id+"F3.opExtrude","SWEPT_EDGE",EDGE,{"disambiguationData":[OSD([subQ1,subQ0]),TDD([makeQuery(id+"F0.imprint","INTERSECT",VERTEX,{"disambiguationData":[OD(1.0)],"derivedFrom":[subQ1,subQ0]})])]});}
            var Q18;
            {var subQ0=sQuery(id+"F0.wireOp",EDGE,"E3.right");var subQ1=sQuery(id+"F0.wireOp",EDGE,"E1.0");Q18=makeQuery(id+"F3.opExtrude","SWEPT_EDGE",EDGE,{"disambiguationData":[OSD([subQ1,subQ0]),TDD([makeQuery(id+"F0.imprint","INTERSECT",VERTEX,{"disambiguationData":[OD(0.0)],"derivedFrom":[subQ1,subQ0]})])]});}
            var Q19;
            {var subQ0=sQuery(id+"F0.wireOp",EDGE,"E2.right");var subQ1=sQuery(id+"F0.wireOp",EDGE,"E1.0");Q19=makeQuery(id+"F3.opExtrude","SWEPT_EDGE",EDGE,{"disambiguationData":[OSD([subQ1,subQ0]),TDD([makeQuery(id+"F0.imprint","INTERSECT",VERTEX,{"disambiguationData":[OD(0.0)],"derivedFrom":[subQ1,subQ0]})])]});}
            var Q20;
            {var subQ0=sQuery(id+"F0.wireOp",EDGE,"E8.left");var subQ1=sQuery(id+"F0.wireOp",EDGE,"E1.0");Q20=makeQuery(id+"F3.opExtrude","SWEPT_EDGE",EDGE,{"disambiguationData":[OSD([subQ1,subQ0]),TDD([makeQuery(id+"F0.imprint","INTERSECT",VERTEX,{"disambiguationData":[OD(1.0)],"derivedFrom":[subQ1,subQ0]})])]});}
            var Q21;
            {var subQ0=sQuery(id+"F0.wireOp",EDGE,"E9.left");var subQ1=sQuery(id+"F0.wireOp",EDGE,"E1.0");Q21=makeQuery(id+"F3.opExtrude","SWEPT_EDGE",EDGE,{"disambiguationData":[OSD([subQ1,subQ0]),TDD([makeQuery(id+"F0.imprint","INTERSECT",VERTEX,{"disambiguationData":[OD(1.0)],"derivedFrom":[subQ1,subQ0]})])]});}
            var Q22;
            {var subQ0=sQuery(id+"F0.wireOp",EDGE,"E7.top");var subQ1=sQuery(id+"F0.wireOp",EDGE,"E1.0");Q22=makeQuery(id+"F3.opExtrude","SWEPT_EDGE",EDGE,{"disambiguationData":[OSD([subQ1,subQ0]),TDD([makeQuery(id+"F0.imprint","INTERSECT",VERTEX,{"disambiguationData":[OD(1.0)],"derivedFrom":[subQ1,subQ0]})])]});}
            var Q23;
            {var subQ0=sQuery(id+"F0.wireOp",EDGE,"E6.bottom");var subQ1=sQuery(id+"F0.wireOp",EDGE,"E1.0");Q23=makeQuery(id+"F3.opExtrude","SWEPT_EDGE",EDGE,{"disambiguationData":[OSD([subQ1,subQ0]),TDD([makeQuery(id+"F0.imprint","INTERSECT",VERTEX,{"disambiguationData":[OD(0.0)],"derivedFrom":[subQ1,subQ0]})])]});}
            var Q24;
            {var subQ0=sQuery(id+"F0.wireOp",EDGE,"E7.top");var subQ1=sQuery(id+"F0.wireOp",EDGE,"E1.0");var subQ17=sQuery(id+"F1.wireOp",EDGE,"E12");Q24=makeQuery(id+"F7.boolean.opBoolean","INTERSECT",EDGE,{"derivedFrom":[makeQuery(id+"F5.boolean.opBoolean","MERGE",FACE,{"derivedFrom":[makeQuery(id+"F3.boolean.opBoolean","SPLIT",FACE,{"disambiguationData":[TD([makeQuery(id+"F3.opExtrude","SWEPT_FACE",FACE,{"disambiguationData":[OSD([subQ0])]})])],"derivedFrom":makeQuery(id+"F2.opExtrude","SWEPT_FACE",FACE,{"disambiguationData":[OSD([subQ17])]})}),makeQuery(id+"F5.opExtrude","SWEPT_FACE",FACE,{"disambiguationData":[OSD([subQ1]),TDD([makeQuery(id+"F0.imprint","IMPRINT",EDGE,{"disambiguationData":[TD([[makeQuery(id+"F0.imprint","INTERSECT",VERTEX,{"disambiguationData":[OD(0.0)],"derivedFrom":[subQ1,subQ0]}),-1.0]])],"derivedFrom":subQ1})])]})]}),makeQuery(id+"F7.opExtrude","SWEPT_FACE",FACE,{"disambiguationData":[OSD([sQuery(id+"F6.wireOp",EDGE,"E30")])]})]});}
            var Q25;
            {var subQ0=sQuery(id+"F0.wireOp",EDGE,"E7.top");Q25=makeQuery(id+"F7.boolean.opBoolean","INTERSECT",EDGE,{"derivedFrom":[makeQuery(id+"F5.boolean.opBoolean","MERGE",FACE,{"derivedFrom":[makeQuery(id+"F3.opExtrude","SWEPT_FACE",FACE,{"disambiguationData":[OSD([subQ0])]}),makeQuery(id+"F5.opExtrude","SWEPT_FACE",FACE,{"disambiguationData":[OSD([subQ0]),TDD([makeQuery(id+"F0.imprint","IMPRINT",EDGE,{"disambiguationData":[TD([[makeQuery(id+"F0.imprint","INTERSECT",VERTEX,{"disambiguationData":[OD(0.0)],"derivedFrom":[sQuery(id+"F0.wireOp",EDGE,"E1.0"),subQ0]}),-1.0]])],"derivedFrom":subQ0})])]})]}),makeQuery(id+"F7.opExtrude","SWEPT_FACE",FACE,{"disambiguationData":[OSD([sQuery(id+"F6.wireOp",EDGE,"E30")])]})]});}
            var Q26;
            {var subQ0=sQuery(id+"F0.wireOp",EDGE,"E2.left");var subQ1=sQuery(id+"F0.wireOp",EDGE,"E1.0");var subQ16=sQuery(id+"F1.wireOp",EDGE,"E12");Q26=makeQuery(id+"F7.boolean.opBoolean","INTERSECT",EDGE,{"derivedFrom":[makeQuery(id+"F5.boolean.opBoolean","MERGE",FACE,{"derivedFrom":[makeQuery(id+"F3.boolean.opBoolean","SPLIT",FACE,{"disambiguationData":[TD([makeQuery(id+"F3.opExtrude","SWEPT_FACE",FACE,{"disambiguationData":[OSD([subQ0])]})])],"derivedFrom":makeQuery(id+"F2.opExtrude","SWEPT_FACE",FACE,{"disambiguationData":[OSD([subQ16])]})}),makeQuery(id+"F5.opExtrude","SWEPT_FACE",FACE,{"disambiguationData":[OSD([subQ1]),TDD([makeQuery(id+"F0.imprint","IMPRINT",EDGE,{"disambiguationData":[TD([[makeQuery(id+"F0.imprint","INTERSECT",VERTEX,{"disambiguationData":[OD(0.0)],"derivedFrom":[subQ1,subQ0]}),-1.0]])],"derivedFrom":subQ1})])]})]}),makeQuery(id+"F7.opExtrude","SWEPT_FACE",FACE,{"disambiguationData":[OSD([sQuery(id+"F6.wireOp",EDGE,"E25")])]})]});}
            var Q27;
            {var subQ0=sQuery(id+"F0.wireOp",EDGE,"E8.right");Q27=makeQuery(id+"F7.boolean.opBoolean","INTERSECT",EDGE,{"derivedFrom":[makeQuery(id+"F5.boolean.opBoolean","MERGE",FACE,{"derivedFrom":[makeQuery(id+"F3.opExtrude","SWEPT_FACE",FACE,{"disambiguationData":[OSD([subQ0]),TDD([makeQuery(id+"F0.imprint","IMPRINT",EDGE,{"disambiguationData":[TD([[makeQuery(id+"F0.imprint","INTERSECT",VERTEX,{"disambiguationData":[OD(0.0)],"derivedFrom":[sQuery(id+"F0.wireOp",EDGE,"E1.0"),subQ0]}),-1.0]])],"derivedFrom":subQ0})])]}),makeQuery(id+"F5.opExtrude","SWEPT_FACE",FACE,{"disambiguationData":[OSD([subQ0])]})]}),makeQuery(id+"F7.opExtrude","SWEPT_FACE",FACE,{"disambiguationData":[OSD([sQuery(id+"F6.wireOp",EDGE,"E25")])]})]});}
            var Q28;
            {var subQ0=sQuery(id+"F0.wireOp",EDGE,"E8.left");var subQ1=sQuery(id+"F0.wireOp",EDGE,"E1.0");var subQ2=makeQuery(id+"F0.imprint","INTERSECT",VERTEX,{"disambiguationData":[OD(0.0)],"derivedFrom":[subQ1,subQ0]});var subQ3=sQuery(id+"F0.wireOp",EDGE,"E9.right");var subQ16=sQuery(id+"F1.wireOp",EDGE,"E12");Q28=makeQuery(id+"F7.boolean.opBoolean","INTERSECT",EDGE,{"derivedFrom":[makeQuery(id+"F5.boolean.opBoolean","MERGE",FACE,{"derivedFrom":[makeQuery(id+"F3.boolean.opBoolean","SPLIT",FACE,{"disambiguationData":[TD([makeQuery(id+"F3.opExtrude","SWEPT_FACE",FACE,{"disambiguationData":[OSD([subQ3])]})])],"derivedFrom":makeQuery(id+"F2.opExtrude","SWEPT_FACE",FACE,{"disambiguationData":[OSD([subQ16])]})}),makeQuery(id+"F5.opExtrude","SWEPT_FACE",FACE,{"disambiguationData":[OSD([subQ1]),TDD([makeQuery(id+"F0.imprint","IMPRINT",EDGE,{"disambiguationData":[TD([[subQ2,-1.0]])],"derivedFrom":subQ1})])]})]}),makeQuery(id+"F7.opExtrude","SWEPT_FACE",FACE,{"disambiguationData":[OSD([sQuery(id+"F6.wireOp",EDGE,"E25")])]})]});}
            var Q29;
            {var subQ0=sQuery(id+"F0.wireOp",EDGE,"E8.left");Q29=makeQuery(id+"F7.boolean.opBoolean","INTERSECT",EDGE,{"derivedFrom":[makeQuery(id+"F5.boolean.opBoolean","MERGE",FACE,{"derivedFrom":[makeQuery(id+"F3.opExtrude","SWEPT_FACE",FACE,{"disambiguationData":[OSD([subQ0]),TDD([makeQuery(id+"F0.imprint","IMPRINT",EDGE,{"disambiguationData":[TD([[makeQuery(id+"F0.imprint","INTERSECT",VERTEX,{"disambiguationData":[OD(0.0)],"derivedFrom":[sQuery(id+"F0.wireOp",EDGE,"E1.0"),subQ0]}),-1.0]])],"derivedFrom":subQ0})])]}),makeQuery(id+"F5.opExtrude","SWEPT_FACE",FACE,{"disambiguationData":[OSD([subQ0])]})]}),makeQuery(id+"F7.opExtrude","SWEPT_FACE",FACE,{"disambiguationData":[OSD([sQuery(id+"F6.wireOp",EDGE,"E25")])]})]});}
            var Q30;
            {var subQ0=sQuery(id+"F0.wireOp",EDGE,"E3.right");Q30=makeQuery(id+"F7.boolean.opBoolean","INTERSECT",EDGE,{"derivedFrom":[makeQuery(id+"F3.opExtrude","SWEPT_FACE",FACE,{"disambiguationData":[OSD([subQ0]),TDD([makeQuery(id+"F0.imprint","IMPRINT",EDGE,{"disambiguationData":[TD([[makeQuery(id+"F0.imprint","INTERSECT",VERTEX,{"disambiguationData":[OD(0.0)],"derivedFrom":[sQuery(id+"F0.wireOp",EDGE,"E1.0"),subQ0]}),-1.0]])],"derivedFrom":subQ0})])]}),makeQuery(id+"F7.opExtrude","SWEPT_FACE",FACE,{"disambiguationData":[OSD([sQuery(id+"F6.wireOp",EDGE,"E26")])]})]});}
            var Q31;
            {var subQ0=sQuery(id+"F0.wireOp",EDGE,"E9.right");var subQ1=sQuery(id+"F0.wireOp",EDGE,"E1.0");var subQ17=sQuery(id+"F1.wireOp",EDGE,"E12");var subQ21=sQuery(id+"F0.wireOp",EDGE,"E3.right");var subQ32=makeQuery(id+"F0.imprint","INTERSECT",VERTEX,{"disambiguationData":[OD(0.0)],"derivedFrom":[subQ1,subQ21]});var subQ33=makeQuery(id+"F0.imprint","IMPRINT",EDGE,{"disambiguationData":[TD([[subQ32,-1.0]])],"derivedFrom":subQ21});Q31=makeQuery(id+"F7.boolean.opBoolean","INTERSECT",EDGE,{"derivedFrom":[makeQuery(id+"F5.boolean.opBoolean","MERGE",FACE,{"derivedFrom":[makeQuery(id+"F3.boolean.opBoolean","SPLIT",FACE,{"disambiguationData":[TD([makeQuery(id+"F3.opExtrude","SWEPT_FACE",FACE,{"disambiguationData":[OSD([subQ21]),TDD([subQ33])]})])],"derivedFrom":makeQuery(id+"F2.opExtrude","SWEPT_FACE",FACE,{"disambiguationData":[OSD([subQ17])]})}),makeQuery(id+"F5.opExtrude","SWEPT_FACE",FACE,{"disambiguationData":[OSD([subQ1]),TDD([makeQuery(id+"F0.imprint","IMPRINT",EDGE,{"disambiguationData":[TD([[makeQuery(id+"F0.imprint","INTERSECT",VERTEX,{"disambiguationData":[OD(1.0)],"derivedFrom":[subQ1,subQ0]}),-1.0]])],"derivedFrom":subQ1})])]})]}),makeQuery(id+"F7.opExtrude","SWEPT_FACE",FACE,{"disambiguationData":[OSD([sQuery(id+"F6.wireOp",EDGE,"E26")])]})]});}
            var Q32;
            {var subQ0=sQuery(id+"F0.wireOp",EDGE,"E3.left");var subQ1=sQuery(id+"F0.wireOp",EDGE,"E1.0");var subQ2=makeQuery(id+"F0.imprint","INTERSECT",VERTEX,{"disambiguationData":[OD(0.0)],"derivedFrom":[subQ1,subQ0]});var subQ3=sQuery(id+"F0.wireOp",EDGE,"E2.right");var subQ18=sQuery(id+"F1.wireOp",EDGE,"E12");Q32=makeQuery(id+"F7.boolean.opBoolean","INTERSECT",EDGE,{"derivedFrom":[makeQuery(id+"F5.boolean.opBoolean","MERGE",FACE,{"derivedFrom":[makeQuery(id+"F3.boolean.opBoolean","SPLIT",FACE,{"disambiguationData":[TD([makeQuery(id+"F3.opExtrude","SWEPT_FACE",FACE,{"disambiguationData":[OSD([subQ3])]})])],"derivedFrom":makeQuery(id+"F2.opExtrude","SWEPT_FACE",FACE,{"disambiguationData":[OSD([subQ18])]})}),makeQuery(id+"F5.opExtrude","SWEPT_FACE",FACE,{"disambiguationData":[OSD([subQ1]),TDD([makeQuery(id+"F0.imprint","IMPRINT",EDGE,{"disambiguationData":[TD([[subQ2,-1.0]])],"derivedFrom":subQ1})])]})]}),makeQuery(id+"F7.opExtrude","SWEPT_FACE",FACE,{"disambiguationData":[OSD([sQuery(id+"F6.wireOp",EDGE,"E26")])]})]});}
            var Q33;
            {var subQ0=sQuery(id+"F0.wireOp",EDGE,"E3.left");Q33=makeQuery(id+"F7.boolean.opBoolean","INTERSECT",EDGE,{"derivedFrom":[makeQuery(id+"F5.boolean.opBoolean","MERGE",FACE,{"derivedFrom":[makeQuery(id+"F3.opExtrude","SWEPT_FACE",FACE,{"disambiguationData":[OSD([subQ0]),TDD([makeQuery(id+"F0.imprint","IMPRINT",EDGE,{"disambiguationData":[TD([[makeQuery(id+"F0.imprint","INTERSECT",VERTEX,{"disambiguationData":[OD(0.0)],"derivedFrom":[sQuery(id+"F0.wireOp",EDGE,"E1.0"),subQ0]}),-1.0]])],"derivedFrom":subQ0})])]}),makeQuery(id+"F5.opExtrude","SWEPT_FACE",FACE,{"disambiguationData":[OSD([subQ0])]})]}),makeQuery(id+"F7.opExtrude","SWEPT_FACE",FACE,{"disambiguationData":[OSD([sQuery(id+"F6.wireOp",EDGE,"E26")])]})]});}
            var Q34;
            {var subQ0=sQuery(id+"F0.wireOp",EDGE,"E9.right");var subQ1=sQuery(id+"F0.wireOp",EDGE,"E1.0");var subQ17=sQuery(id+"F1.wireOp",EDGE,"E12");var subQ21=sQuery(id+"F0.wireOp",EDGE,"E3.right");var subQ32=makeQuery(id+"F0.imprint","INTERSECT",VERTEX,{"disambiguationData":[OD(0.0)],"derivedFrom":[subQ1,subQ21]});var subQ33=makeQuery(id+"F0.imprint","IMPRINT",EDGE,{"disambiguationData":[TD([[subQ32,-1.0]])],"derivedFrom":subQ21});Q34=makeQuery(id+"F7.boolean.opBoolean","INTERSECT",EDGE,{"disambiguationData":[OD(1.0)],"derivedFrom":[makeQuery(id+"F5.boolean.opBoolean","MERGE",FACE,{"derivedFrom":[makeQuery(id+"F3.boolean.opBoolean","SPLIT",FACE,{"disambiguationData":[TD([makeQuery(id+"F3.opExtrude","SWEPT_FACE",FACE,{"disambiguationData":[OSD([subQ21]),TDD([subQ33])]})])],"derivedFrom":makeQuery(id+"F2.opExtrude","SWEPT_FACE",FACE,{"disambiguationData":[OSD([subQ17])]})}),makeQuery(id+"F5.opExtrude","SWEPT_FACE",FACE,{"disambiguationData":[OSD([subQ1]),TDD([makeQuery(id+"F0.imprint","IMPRINT",EDGE,{"disambiguationData":[TD([[makeQuery(id+"F0.imprint","INTERSECT",VERTEX,{"disambiguationData":[OD(1.0)],"derivedFrom":[subQ1,subQ0]}),-1.0]])],"derivedFrom":subQ1})])]})]}),makeQuery(id+"F7.opExtrude","SWEPT_FACE",FACE,{"disambiguationData":[OSD([sQuery(id+"F6.wireOp",EDGE,"E27")])]})]});}
            var Q35;
            {var subQ0=sQuery(id+"F0.wireOp",EDGE,"E9.right");var subQ1=sQuery(id+"F0.wireOp",EDGE,"E1.0");Q35=makeQuery(id+"F5.boolean.opBoolean","COPY",EDGE,{"derivedFrom":makeQuery(id+"F5.opExtrude","SWEPT_EDGE",EDGE,{"disambiguationData":[OSD([subQ1,subQ0]),TDD([makeQuery(id+"F0.imprint","INTERSECT",VERTEX,{"disambiguationData":[OD(1.0)],"derivedFrom":[subQ1,subQ0]})])]})});}
            var Q36;
            {var subQ0=sQuery(id+"F0.wireOp",EDGE,"E9.right");var subQ1=sQuery(id+"F0.wireOp",EDGE,"E1.0");var subQ17=sQuery(id+"F1.wireOp",EDGE,"E12");var subQ21=sQuery(id+"F0.wireOp",EDGE,"E3.right");var subQ32=makeQuery(id+"F0.imprint","INTERSECT",VERTEX,{"disambiguationData":[OD(0.0)],"derivedFrom":[subQ1,subQ21]});var subQ33=makeQuery(id+"F0.imprint","IMPRINT",EDGE,{"disambiguationData":[TD([[subQ32,-1.0]])],"derivedFrom":subQ21});Q36=makeQuery(id+"F7.boolean.opBoolean","INTERSECT",EDGE,{"disambiguationData":[OD(0.0)],"derivedFrom":[makeQuery(id+"F5.boolean.opBoolean","MERGE",FACE,{"derivedFrom":[makeQuery(id+"F3.boolean.opBoolean","SPLIT",FACE,{"disambiguationData":[TD([makeQuery(id+"F3.opExtrude","SWEPT_FACE",FACE,{"disambiguationData":[OSD([subQ21]),TDD([subQ33])]})])],"derivedFrom":makeQuery(id+"F2.opExtrude","SWEPT_FACE",FACE,{"disambiguationData":[OSD([subQ17])]})}),makeQuery(id+"F5.opExtrude","SWEPT_FACE",FACE,{"disambiguationData":[OSD([subQ1]),TDD([makeQuery(id+"F0.imprint","IMPRINT",EDGE,{"disambiguationData":[TD([[makeQuery(id+"F0.imprint","INTERSECT",VERTEX,{"disambiguationData":[OD(1.0)],"derivedFrom":[subQ1,subQ0]}),-1.0]])],"derivedFrom":subQ1})])]})]}),makeQuery(id+"F7.opExtrude","SWEPT_FACE",FACE,{"disambiguationData":[OSD([sQuery(id+"F6.wireOp",EDGE,"E27")])]})]});}
            var Q37;
            {var subQ0=sQuery(id+"F0.wireOp",EDGE,"E7.top");Q37=makeQuery(id+"F7.boolean.opBoolean","INTERSECT",EDGE,{"derivedFrom":[makeQuery(id+"F5.boolean.opBoolean","COPY",FACE,{"derivedFrom":makeQuery(id+"F5.opExtrude","SWEPT_FACE",FACE,{"disambiguationData":[OSD([subQ0]),TDD([makeQuery(id+"F0.imprint","IMPRINT",EDGE,{"disambiguationData":[TD([[makeQuery(id+"F0.imprint","INTERSECT",VERTEX,{"disambiguationData":[OD(1.0)],"derivedFrom":[sQuery(id+"F0.wireOp",EDGE,"E1.0"),subQ0]}),1.0]])],"derivedFrom":subQ0})])]})}),makeQuery(id+"F7.opExtrude","SWEPT_FACE",FACE,{"disambiguationData":[OSD([sQuery(id+"F6.wireOp",EDGE,"E27")])]})]});}
            var Q38;
            {var subQ0=sQuery(id+"F0.wireOp",EDGE,"E8.left");Q38=makeQuery(id+"F7.boolean.opBoolean","INTERSECT",EDGE,{"derivedFrom":[makeQuery(id+"F3.opExtrude","SWEPT_FACE",FACE,{"disambiguationData":[OSD([subQ0]),TDD([makeQuery(id+"F0.imprint","IMPRINT",EDGE,{"disambiguationData":[TD([[makeQuery(id+"F0.imprint","INTERSECT",VERTEX,{"disambiguationData":[OD(1.0)],"derivedFrom":[sQuery(id+"F0.wireOp",EDGE,"E1.0"),subQ0]}),1.0]])],"derivedFrom":subQ0})])]}),makeQuery(id+"F7.opExtrude","SWEPT_FACE",FACE,{"disambiguationData":[OSD([sQuery(id+"F6.wireOp",EDGE,"E28")])]})]});}
            var Q39;
            {var subQ0=sQuery(id+"F0.wireOp",EDGE,"E3.right");var subQ1=sQuery(id+"F0.wireOp",EDGE,"E1.0");var subQ2=makeQuery(id+"F0.imprint","INTERSECT",VERTEX,{"disambiguationData":[OD(1.0)],"derivedFrom":[subQ1,subQ0]});var subQ21=sQuery(id+"F1.wireOp",EDGE,"E12");var subQ27=makeQuery(id+"F0.imprint","IMPRINT",EDGE,{"disambiguationData":[TD([[subQ2,1.0]])],"derivedFrom":subQ0});Q39=makeQuery(id+"F7.boolean.opBoolean","INTERSECT",EDGE,{"derivedFrom":[makeQuery(id+"F5.boolean.opBoolean","MERGE",FACE,{"derivedFrom":[makeQuery(id+"F3.boolean.opBoolean","SPLIT",FACE,{"disambiguationData":[TD([makeQuery(id+"F3.opExtrude","SWEPT_FACE",FACE,{"disambiguationData":[OSD([subQ0]),TDD([subQ27])]})])],"derivedFrom":makeQuery(id+"F2.opExtrude","SWEPT_FACE",FACE,{"disambiguationData":[OSD([subQ21])]})}),makeQuery(id+"F5.opExtrude","SWEPT_FACE",FACE,{"disambiguationData":[OSD([subQ1]),TDD([makeQuery(id+"F0.imprint","IMPRINT",EDGE,{"disambiguationData":[TD([[subQ2,-1.0]])],"derivedFrom":subQ1})])]})]}),makeQuery(id+"F7.opExtrude","SWEPT_FACE",FACE,{"disambiguationData":[OSD([sQuery(id+"F6.wireOp",EDGE,"E28")])]})]});}
            var Q40;
            {var subQ0=sQuery(id+"F0.wireOp",EDGE,"E9.right");var subQ1=sQuery(id+"F0.wireOp",EDGE,"E1.0");var subQ17=sQuery(id+"F1.wireOp",EDGE,"E12");var subQ21=sQuery(id+"F0.wireOp",EDGE,"E3.right");var subQ32=makeQuery(id+"F0.imprint","INTERSECT",VERTEX,{"disambiguationData":[OD(0.0)],"derivedFrom":[subQ1,subQ21]});var subQ33=makeQuery(id+"F0.imprint","IMPRINT",EDGE,{"disambiguationData":[TD([[subQ32,-1.0]])],"derivedFrom":subQ21});Q40=makeQuery(id+"F7.boolean.opBoolean","INTERSECT",EDGE,{"derivedFrom":[makeQuery(id+"F5.boolean.opBoolean","MERGE",FACE,{"derivedFrom":[makeQuery(id+"F3.boolean.opBoolean","SPLIT",FACE,{"disambiguationData":[TD([makeQuery(id+"F3.opExtrude","SWEPT_FACE",FACE,{"disambiguationData":[OSD([subQ21]),TDD([subQ33])]})])],"derivedFrom":makeQuery(id+"F2.opExtrude","SWEPT_FACE",FACE,{"disambiguationData":[OSD([subQ17])]})}),makeQuery(id+"F5.opExtrude","SWEPT_FACE",FACE,{"disambiguationData":[OSD([subQ1]),TDD([makeQuery(id+"F0.imprint","IMPRINT",EDGE,{"disambiguationData":[TD([[makeQuery(id+"F0.imprint","INTERSECT",VERTEX,{"disambiguationData":[OD(1.0)],"derivedFrom":[subQ1,subQ0]}),-1.0]])],"derivedFrom":subQ1})])]})]}),makeQuery(id+"F7.opExtrude","SWEPT_FACE",FACE,{"disambiguationData":[OSD([sQuery(id+"F6.wireOp",EDGE,"E28")])]})]});}
            var Q41;
            {var subQ0=sQuery(id+"F0.wireOp",EDGE,"E8.right");Q41=makeQuery(id+"F7.boolean.opBoolean","INTERSECT",EDGE,{"derivedFrom":[makeQuery(id+"F3.opExtrude","SWEPT_FACE",FACE,{"disambiguationData":[OSD([subQ0]),TDD([makeQuery(id+"F0.imprint","IMPRINT",EDGE,{"disambiguationData":[TD([[makeQuery(id+"F0.imprint","INTERSECT",VERTEX,{"disambiguationData":[OD(1.0)],"derivedFrom":[sQuery(id+"F0.wireOp",EDGE,"E1.0"),subQ0]}),1.0]])],"derivedFrom":subQ0})])]}),makeQuery(id+"F7.opExtrude","SWEPT_FACE",FACE,{"disambiguationData":[OSD([sQuery(id+"F6.wireOp",EDGE,"E28")])]})]});}
            var Q42;
            {var subQ0=sQuery(id+"F0.wireOp",EDGE,"E2.left");var subQ1=sQuery(id+"F0.wireOp",EDGE,"E1.0");Q42=makeQuery(id+"F5.boolean.opBoolean","COPY",EDGE,{"derivedFrom":makeQuery(id+"F5.opExtrude","SWEPT_EDGE",EDGE,{"disambiguationData":[OSD([subQ1,subQ0]),TDD([makeQuery(id+"F0.imprint","INTERSECT",VERTEX,{"disambiguationData":[OD(1.0)],"derivedFrom":[subQ1,subQ0]})])]})});}
            var Q43;
            {var subQ0=sQuery(id+"F0.wireOp",EDGE,"E7.top");var subQ1=sQuery(id+"F0.wireOp",EDGE,"E1.0");var subQ17=sQuery(id+"F1.wireOp",EDGE,"E12");Q43=makeQuery(id+"F7.boolean.opBoolean","INTERSECT",EDGE,{"derivedFrom":[makeQuery(id+"F5.boolean.opBoolean","MERGE",FACE,{"derivedFrom":[makeQuery(id+"F3.boolean.opBoolean","SPLIT",FACE,{"disambiguationData":[TD([makeQuery(id+"F3.opExtrude","SWEPT_FACE",FACE,{"disambiguationData":[OSD([subQ0])]})])],"derivedFrom":makeQuery(id+"F2.opExtrude","SWEPT_FACE",FACE,{"disambiguationData":[OSD([subQ17])]})}),makeQuery(id+"F5.opExtrude","SWEPT_FACE",FACE,{"disambiguationData":[OSD([subQ1]),TDD([makeQuery(id+"F0.imprint","IMPRINT",EDGE,{"disambiguationData":[TD([[makeQuery(id+"F0.imprint","INTERSECT",VERTEX,{"disambiguationData":[OD(0.0)],"derivedFrom":[subQ1,subQ0]}),-1.0]])],"derivedFrom":subQ1})])]})]}),makeQuery(id+"F7.opExtrude","SWEPT_FACE",FACE,{"disambiguationData":[OSD([sQuery(id+"F6.wireOp",EDGE,"E29")])]})]});}
            var Q44;
            {var subQ0=sQuery(id+"F0.wireOp",EDGE,"E3.left");Q44=makeQuery(id+"F7.boolean.opBoolean","INTERSECT",EDGE,{"derivedFrom":[makeQuery(id+"F3.opExtrude","SWEPT_FACE",FACE,{"disambiguationData":[OSD([subQ0]),TDD([makeQuery(id+"F0.imprint","IMPRINT",EDGE,{"disambiguationData":[TD([[makeQuery(id+"F0.imprint","INTERSECT",VERTEX,{"disambiguationData":[OD(1.0)],"derivedFrom":[sQuery(id+"F0.wireOp",EDGE,"E1.0"),subQ0]}),1.0]])],"derivedFrom":subQ0})])]}),makeQuery(id+"F7.opExtrude","SWEPT_FACE",FACE,{"disambiguationData":[OSD([sQuery(id+"F6.wireOp",EDGE,"E29")])]})]});}
            var Q45;
            {var subQ0=sQuery(id+"F0.wireOp",EDGE,"E3.right");Q45=makeQuery(id+"F7.boolean.opBoolean","INTERSECT",EDGE,{"derivedFrom":[makeQuery(id+"F5.boolean.opBoolean","MERGE",FACE,{"derivedFrom":[makeQuery(id+"F3.opExtrude","SWEPT_FACE",FACE,{"disambiguationData":[OSD([subQ0]),TDD([makeQuery(id+"F0.imprint","IMPRINT",EDGE,{"disambiguationData":[TD([[makeQuery(id+"F0.imprint","INTERSECT",VERTEX,{"disambiguationData":[OD(1.0)],"derivedFrom":[sQuery(id+"F0.wireOp",EDGE,"E1.0"),subQ0]}),1.0]])],"derivedFrom":subQ0})])]}),makeQuery(id+"F5.opExtrude","SWEPT_FACE",FACE,{"disambiguationData":[OSD([subQ0])]})]}),makeQuery(id+"F7.opExtrude","SWEPT_FACE",FACE,{"disambiguationData":[OSD([sQuery(id+"F6.wireOp",EDGE,"E29")])]})]});}
            var Q46;
            {var subQ0=sQuery(id+"F0.wireOp",EDGE,"E3.right");var subQ1=sQuery(id+"F0.wireOp",EDGE,"E1.0");var subQ2=makeQuery(id+"F0.imprint","INTERSECT",VERTEX,{"disambiguationData":[OD(1.0)],"derivedFrom":[subQ1,subQ0]});var subQ21=sQuery(id+"F1.wireOp",EDGE,"E12");var subQ27=makeQuery(id+"F0.imprint","IMPRINT",EDGE,{"disambiguationData":[TD([[subQ2,1.0]])],"derivedFrom":subQ0});Q46=makeQuery(id+"F7.boolean.opBoolean","INTERSECT",EDGE,{"derivedFrom":[makeQuery(id+"F5.boolean.opBoolean","MERGE",FACE,{"derivedFrom":[makeQuery(id+"F3.boolean.opBoolean","SPLIT",FACE,{"disambiguationData":[TD([makeQuery(id+"F3.opExtrude","SWEPT_FACE",FACE,{"disambiguationData":[OSD([subQ0]),TDD([subQ27])]})])],"derivedFrom":makeQuery(id+"F2.opExtrude","SWEPT_FACE",FACE,{"disambiguationData":[OSD([subQ21])]})}),makeQuery(id+"F5.opExtrude","SWEPT_FACE",FACE,{"disambiguationData":[OSD([subQ1]),TDD([makeQuery(id+"F0.imprint","IMPRINT",EDGE,{"disambiguationData":[TD([[subQ2,-1.0]])],"derivedFrom":subQ1})])]})]}),makeQuery(id+"F7.opExtrude","SWEPT_FACE",FACE,{"disambiguationData":[OSD([sQuery(id+"F6.wireOp",EDGE,"E29")])]})]});}
            var Q47;
            Q47=makeQuery(id+"F5.boolean.opBoolean","COPY",EDGE,{"derivedFrom":makeQuery(id+"F5.opExtrude","SWEPT_EDGE",EDGE,{"disambiguationData":[OSD([sQuery(id+"F0.wireOp",EDGE,"E1.0"),sQuery(id+"F0.wireOp",EDGE,"E6.bottom")])]})});
            var Q48;
            {var subQ0=sQuery(id+"F0.wireOp",EDGE,"E9.left");var subQ1=sQuery(id+"F0.wireOp",EDGE,"E1.0");var subQ2=sQuery(id+"F0.wireOp",EDGE,"E7.bottom");var subQ17=sQuery(id+"F1.wireOp",EDGE,"E12");Q48=makeQuery(id+"F7.boolean.opBoolean","INTERSECT",EDGE,{"derivedFrom":[makeQuery(id+"F5.boolean.opBoolean","MERGE",FACE,{"derivedFrom":[makeQuery(id+"F3.boolean.opBoolean","SPLIT",FACE,{"disambiguationData":[TD([makeQuery(id+"F3.opExtrude","SWEPT_FACE",FACE,{"disambiguationData":[OSD([subQ2])]})])],"derivedFrom":makeQuery(id+"F2.opExtrude","SWEPT_FACE",FACE,{"disambiguationData":[OSD([subQ17])]})}),makeQuery(id+"F5.opExtrude","SWEPT_FACE",FACE,{"disambiguationData":[OSD([subQ1]),TDD([makeQuery(id+"F0.imprint","IMPRINT",EDGE,{"disambiguationData":[TD([[makeQuery(id+"F0.imprint","INTERSECT",VERTEX,{"disambiguationData":[OD(0.0)],"derivedFrom":[subQ1,subQ0]}),-1.0]])],"derivedFrom":subQ1})])]})]}),makeQuery(id+"F7.opExtrude","SWEPT_FACE",FACE,{"disambiguationData":[OSD([sQuery(id+"F6.wireOp",EDGE,"E30")])]})]});}
            var Q49;
            {var subQ0=sQuery(id+"F0.wireOp",EDGE,"E7.bottom");Q49=makeQuery(id+"F7.boolean.opBoolean","INTERSECT",EDGE,{"derivedFrom":[makeQuery(id+"F5.boolean.opBoolean","MERGE",FACE,{"derivedFrom":[makeQuery(id+"F3.opExtrude","SWEPT_FACE",FACE,{"disambiguationData":[OSD([subQ0])]}),makeQuery(id+"F5.opExtrude","SWEPT_FACE",FACE,{"disambiguationData":[OSD([subQ0])]})]}),makeQuery(id+"F7.opExtrude","SWEPT_FACE",FACE,{"disambiguationData":[OSD([sQuery(id+"F6.wireOp",EDGE,"E30")])]})]});}
            fillet(context, id + "F8", {"entities" : qUnion([Q0, Q1, Q2, Q3, Q4, Q5, Q6, Q7, Q8, Q9, Q10, Q11, Q12, Q13, Q14, Q15, Q16, Q17, Q18, Q19, Q20, Q21, Q22, Q23, Q24, Q25, Q26, Q27, Q28, Q29, Q30, Q31, Q32, Q33, Q34, Q35, Q36, Q37, Q38, Q39, Q40, Q41, Q42, Q43, Q44, Q45, Q46, Q47, Q48, Q49]), "radius" : 1 * mm, "tangentPropagation" : true, "allowEdgeOverflow" : false});
        }
        {
            var Q0;
            {var subQ0=sQuery(id+"F6.wireOp",EDGE,"E31");var subQ1=sQuery(id+"F6.wireOp",EDGE,"E13");var subQ2=makeQuery(id+"F6.imprint","INTERSECT",VERTEX,{"disambiguationData":[OD(0.0)],"derivedFrom":[subQ1,subQ0]});Q0=makeQuery(id+"F6.imprint","IMPRINT",FACE,{"disambiguationData":[TD([[makeQuery(id+"F6.imprint","IMPRINT",EDGE,{"disambiguationData":[TD([[subQ2,-1.0]])],"derivedFrom":subQ1}),-1.0]])]});}
            var Q1;
            {var subQ0=sQuery(id+"F6.wireOp",EDGE,"E31");var subQ1=sQuery(id+"F6.wireOp",EDGE,"E13");var subQ2=makeQuery(id+"F6.imprint","INTERSECT",VERTEX,{"disambiguationData":[OD(0.0)],"derivedFrom":[subQ1,subQ0]});Q1=makeQuery(id+"F6.imprint","IMPRINT",FACE,{"disambiguationData":[TD([[makeQuery(id+"F6.imprint","IMPRINT",EDGE,{"disambiguationData":[TD([[subQ2,-1.0]])],"derivedFrom":subQ1}),1.0]])]});}
            var Q2;
            {var subQ0=sQuery(id+"F6.wireOp",EDGE,"E32");var subQ1=sQuery(id+"F6.wireOp",EDGE,"E13");var subQ2=makeQuery(id+"F6.imprint","INTERSECT",VERTEX,{"disambiguationData":[OD(0.0)],"derivedFrom":[subQ1,subQ0]});Q2=makeQuery(id+"F6.imprint","IMPRINT",FACE,{"disambiguationData":[TD([[makeQuery(id+"F6.imprint","IMPRINT",EDGE,{"disambiguationData":[TD([[subQ2,-1.0]])],"derivedFrom":subQ1}),-1.0]])]});}
            var Q3;
            {var subQ0=sQuery(id+"F6.wireOp",EDGE,"E32");var subQ1=sQuery(id+"F6.wireOp",EDGE,"E13");var subQ2=makeQuery(id+"F6.imprint","INTERSECT",VERTEX,{"disambiguationData":[OD(0.0)],"derivedFrom":[subQ1,subQ0]});Q3=makeQuery(id+"F6.imprint","IMPRINT",FACE,{"disambiguationData":[TD([[makeQuery(id+"F6.imprint","IMPRINT",EDGE,{"disambiguationData":[TD([[subQ2,-1.0]])],"derivedFrom":subQ1}),1.0]])]});}
            var Q4;
            {var subQ0=sQuery(id+"F6.wireOp",EDGE,"E33");var subQ1=sQuery(id+"F6.wireOp",EDGE,"E13");var subQ2=makeQuery(id+"F6.imprint","INTERSECT",VERTEX,{"disambiguationData":[OD(0.0)],"derivedFrom":[subQ1,subQ0]});Q4=makeQuery(id+"F6.imprint","IMPRINT",FACE,{"disambiguationData":[TD([[makeQuery(id+"F6.imprint","IMPRINT",EDGE,{"disambiguationData":[TD([[subQ2,-1.0]])],"derivedFrom":subQ1}),1.0]])]});}
            var Q5;
            {var subQ0=sQuery(id+"F6.wireOp",EDGE,"E33");var subQ1=sQuery(id+"F6.wireOp",EDGE,"E13");var subQ2=makeQuery(id+"F6.imprint","INTERSECT",VERTEX,{"disambiguationData":[OD(0.0)],"derivedFrom":[subQ1,subQ0]});Q5=makeQuery(id+"F6.imprint","IMPRINT",FACE,{"disambiguationData":[TD([[makeQuery(id+"F6.imprint","IMPRINT",EDGE,{"disambiguationData":[TD([[subQ2,-1.0]])],"derivedFrom":subQ1}),-1.0]])]});}
            var Q6;
            {var subQ0=sQuery(id+"F6.wireOp",EDGE,"E34");var subQ1=sQuery(id+"F6.wireOp",EDGE,"E13");var subQ2=makeQuery(id+"F6.imprint","INTERSECT",VERTEX,{"disambiguationData":[OD(0.0)],"derivedFrom":[subQ1,subQ0]});Q6=makeQuery(id+"F6.imprint","IMPRINT",FACE,{"disambiguationData":[TD([[makeQuery(id+"F6.imprint","IMPRINT",EDGE,{"disambiguationData":[TD([[subQ2,-1.0]])],"derivedFrom":subQ1}),1.0]])]});}
            var Q7;
            {var subQ0=sQuery(id+"F6.wireOp",EDGE,"E34");var subQ1=sQuery(id+"F6.wireOp",EDGE,"E13");var subQ2=makeQuery(id+"F6.imprint","INTERSECT",VERTEX,{"disambiguationData":[OD(0.0)],"derivedFrom":[subQ1,subQ0]});Q7=makeQuery(id+"F6.imprint","IMPRINT",FACE,{"disambiguationData":[TD([[makeQuery(id+"F6.imprint","IMPRINT",EDGE,{"disambiguationData":[TD([[subQ2,-1.0]])],"derivedFrom":subQ1}),-1.0]])]});}
            var Q8;
            {var subQ1=sQuery(id+"F6.wireOp",EDGE,"E36.bottom");Q8=makeQuery(id+"F6.imprint","IMPRINT",FACE,{"disambiguationData":[TD([[makeQuery(id+"F6.imprint","IMPRINT",EDGE,{"derivedFrom":subQ1}),-1.0]])]});}
            var Q9;
            {var subQ0=sQuery(id+"F6.wireOp",EDGE,"E36.top");var subQ1=sQuery(id+"F6.wireOp",EDGE,"E13");var subQ2=makeQuery(id+"F6.imprint","INTERSECT",VERTEX,{"derivedFrom":[subQ1,subQ0]});Q9=makeQuery(id+"F6.imprint","IMPRINT",FACE,{"disambiguationData":[TD([[makeQuery(id+"F6.imprint","IMPRINT",EDGE,{"disambiguationData":[TD([[subQ2,-1.0]])],"derivedFrom":subQ1}),1.0]])]});}
            var Q10;
            {var subQ0=sQuery(id+"F6.wireOp",EDGE,"E35");var subQ1=sQuery(id+"F6.wireOp",EDGE,"E13");var subQ2=makeQuery(id+"F6.imprint","INTERSECT",VERTEX,{"disambiguationData":[OD(0.0)],"derivedFrom":[subQ1,subQ0]});Q10=makeQuery(id+"F6.imprint","IMPRINT",FACE,{"disambiguationData":[TD([[makeQuery(id+"F6.imprint","IMPRINT",EDGE,{"disambiguationData":[TD([[subQ2,-1.0]])],"derivedFrom":subQ1}),-1.0]])]});}
            var Q11;
            {var subQ0=sQuery(id+"F6.wireOp",EDGE,"E35");var subQ1=sQuery(id+"F6.wireOp",EDGE,"E13");var subQ2=makeQuery(id+"F6.imprint","INTERSECT",VERTEX,{"disambiguationData":[OD(0.0)],"derivedFrom":[subQ1,subQ0]});Q11=makeQuery(id+"F6.imprint","IMPRINT",FACE,{"disambiguationData":[TD([[makeQuery(id+"F6.imprint","IMPRINT",EDGE,{"disambiguationData":[TD([[subQ2,-1.0]])],"derivedFrom":subQ1}),1.0]])]});}
            extrude(context, id + "F9", {"entities" : qUnion([Q0, Q1, Q2, Q3, Q4, Q5, Q6, Q7, Q8, Q9, Q10, Q11]), "operationType" : NewBodyOperationType.ADD, "depth" : 11 * mm, "offsetDistance" : 25 * mm, "hasDraft" : true, "draftAngle" : .9 * degree, "draftPullDirection" : true});
        }
        {
            var Q0;
            Q0=makeQuery(id+"F9.opExtrude","CAP_EDGE",EDGE,{"disambiguationData":[OSD([sQuery(id+"F6.wireOp",EDGE,"E35")])],"isStart":false});
            var Q1;
            Q1=makeQuery(id+"F9.opExtrude","CAP_FACE",FACE,{"disambiguationData":[OSD([sQuery(id+"F6.wireOp",EDGE,"E31")])],"isStart":false});
            var Q2;
            Q2=makeQuery(id+"F9.opExtrude","CAP_FACE",FACE,{"disambiguationData":[OSD([sQuery(id+"F6.wireOp",EDGE,"E32")])],"isStart":false});
            var Q3;
            Q3=makeQuery(id+"F9.opExtrude","CAP_FACE",FACE,{"disambiguationData":[OSD([sQuery(id+"F6.wireOp",EDGE,"E33")])],"isStart":false});
            var Q4;
            Q4=makeQuery(id+"F9.opExtrude","CAP_FACE",FACE,{"disambiguationData":[OSD([sQuery(id+"F6.wireOp",EDGE,"E34")])],"isStart":false});
            var Q5;
            Q5=makeQuery(id+"F9.opExtrude","CAP_EDGE",EDGE,{"disambiguationData":[OSD([sQuery(id+"F6.wireOp",EDGE,"E36.left")])],"isStart":false});
            var Q6;
            Q6=makeQuery(id+"F9.opExtrude","CAP_EDGE",EDGE,{"disambiguationData":[OSD([sQuery(id+"F6.wireOp",EDGE,"E36.right")])],"isStart":false});
            var Q7;
            Q7=makeQuery(id+"F9.opExtrude","CAP_EDGE",EDGE,{"disambiguationData":[OSD([sQuery(id+"F6.wireOp",EDGE,"E36.bottom")])],"isStart":false});
            var Q8;
            Q8=makeQuery(id+"F9.opExtrude","CAP_EDGE",EDGE,{"disambiguationData":[OSD([sQuery(id+"F6.wireOp",EDGE,"E36.top")])],"isStart":false});
            fillet(context, id + "F10", {"entities" : qUnion([Q0, Q1, Q2, Q3, Q4, Q5, Q6, Q7, Q8]), "radius" : .45 * mm, "tangentPropagation" : true, "allowEdgeOverflow" : false});
        }
        {
            var Q0;
            {var subQ0=sQuery(id+"F6.wireOp",EDGE,"E35");var subQ1=sQuery(id+"F6.wireOp",EDGE,"E13");var subQ2=makeQuery(id+"F6.imprint","INTERSECT",VERTEX,{"disambiguationData":[OD(0.0)],"derivedFrom":[subQ1,subQ0]});Q0=makeQuery(id+"F6.imprint","IMPRINT",FACE,{"disambiguationData":[TD([[makeQuery(id+"F6.imprint","IMPRINT",EDGE,{"disambiguationData":[TD([[subQ2,-1.0]])],"derivedFrom":subQ1}),-1.0]])]});}
            var Q1;
            {var subQ0=sQuery(id+"F6.wireOp",EDGE,"E35");var subQ1=sQuery(id+"F6.wireOp",EDGE,"E13");var subQ2=makeQuery(id+"F6.imprint","INTERSECT",VERTEX,{"disambiguationData":[OD(0.0)],"derivedFrom":[subQ1,subQ0]});Q1=makeQuery(id+"F6.imprint","IMPRINT",FACE,{"disambiguationData":[TD([[makeQuery(id+"F6.imprint","IMPRINT",EDGE,{"disambiguationData":[TD([[subQ2,-1.0]])],"derivedFrom":subQ1}),1.0]])]});}
            var Q2;
            {var subQ1=sQuery(id+"F6.wireOp",EDGE,"E36.bottom");Q2=makeQuery(id+"F6.imprint","IMPRINT",FACE,{"disambiguationData":[TD([[makeQuery(id+"F6.imprint","IMPRINT",EDGE,{"derivedFrom":subQ1}),-1.0]])]});}
            var Q3;
            {var subQ0=sQuery(id+"F6.wireOp",EDGE,"E36.top");var subQ1=sQuery(id+"F6.wireOp",EDGE,"E13");var subQ2=makeQuery(id+"F6.imprint","INTERSECT",VERTEX,{"derivedFrom":[subQ1,subQ0]});Q3=makeQuery(id+"F6.imprint","IMPRINT",FACE,{"disambiguationData":[TD([[makeQuery(id+"F6.imprint","IMPRINT",EDGE,{"disambiguationData":[TD([[subQ2,-1.0]])],"derivedFrom":subQ1}),1.0]])]});}
            var Q4;
            {var subQ0=sQuery(id+"F6.wireOp",EDGE,"E34");var subQ1=sQuery(id+"F6.wireOp",EDGE,"E13");var subQ2=makeQuery(id+"F6.imprint","INTERSECT",VERTEX,{"disambiguationData":[OD(0.0)],"derivedFrom":[subQ1,subQ0]});Q4=makeQuery(id+"F6.imprint","IMPRINT",FACE,{"disambiguationData":[TD([[makeQuery(id+"F6.imprint","IMPRINT",EDGE,{"disambiguationData":[TD([[subQ2,-1.0]])],"derivedFrom":subQ1}),1.0]])]});}
            var Q5;
            {var subQ0=sQuery(id+"F6.wireOp",EDGE,"E34");var subQ1=sQuery(id+"F6.wireOp",EDGE,"E13");var subQ2=makeQuery(id+"F6.imprint","INTERSECT",VERTEX,{"disambiguationData":[OD(0.0)],"derivedFrom":[subQ1,subQ0]});Q5=makeQuery(id+"F6.imprint","IMPRINT",FACE,{"disambiguationData":[TD([[makeQuery(id+"F6.imprint","IMPRINT",EDGE,{"disambiguationData":[TD([[subQ2,-1.0]])],"derivedFrom":subQ1}),-1.0]])]});}
            var Q6;
            {var subQ0=sQuery(id+"F6.wireOp",EDGE,"E33");var subQ1=sQuery(id+"F6.wireOp",EDGE,"E13");var subQ2=makeQuery(id+"F6.imprint","INTERSECT",VERTEX,{"disambiguationData":[OD(0.0)],"derivedFrom":[subQ1,subQ0]});Q6=makeQuery(id+"F6.imprint","IMPRINT",FACE,{"disambiguationData":[TD([[makeQuery(id+"F6.imprint","IMPRINT",EDGE,{"disambiguationData":[TD([[subQ2,-1.0]])],"derivedFrom":subQ1}),1.0]])]});}
            var Q7;
            {var subQ0=sQuery(id+"F6.wireOp",EDGE,"E33");var subQ1=sQuery(id+"F6.wireOp",EDGE,"E13");var subQ2=makeQuery(id+"F6.imprint","INTERSECT",VERTEX,{"disambiguationData":[OD(0.0)],"derivedFrom":[subQ1,subQ0]});Q7=makeQuery(id+"F6.imprint","IMPRINT",FACE,{"disambiguationData":[TD([[makeQuery(id+"F6.imprint","IMPRINT",EDGE,{"disambiguationData":[TD([[subQ2,-1.0]])],"derivedFrom":subQ1}),-1.0]])]});}
            var Q8;
            {var subQ0=sQuery(id+"F6.wireOp",EDGE,"E32");var subQ1=sQuery(id+"F6.wireOp",EDGE,"E13");var subQ2=makeQuery(id+"F6.imprint","INTERSECT",VERTEX,{"disambiguationData":[OD(0.0)],"derivedFrom":[subQ1,subQ0]});Q8=makeQuery(id+"F6.imprint","IMPRINT",FACE,{"disambiguationData":[TD([[makeQuery(id+"F6.imprint","IMPRINT",EDGE,{"disambiguationData":[TD([[subQ2,-1.0]])],"derivedFrom":subQ1}),1.0]])]});}
            var Q9;
            {var subQ0=sQuery(id+"F6.wireOp",EDGE,"E32");var subQ1=sQuery(id+"F6.wireOp",EDGE,"E13");var subQ2=makeQuery(id+"F6.imprint","INTERSECT",VERTEX,{"disambiguationData":[OD(0.0)],"derivedFrom":[subQ1,subQ0]});Q9=makeQuery(id+"F6.imprint","IMPRINT",FACE,{"disambiguationData":[TD([[makeQuery(id+"F6.imprint","IMPRINT",EDGE,{"disambiguationData":[TD([[subQ2,-1.0]])],"derivedFrom":subQ1}),-1.0]])]});}
            var Q10;
            {var subQ0=sQuery(id+"F6.wireOp",EDGE,"E31");var subQ1=sQuery(id+"F6.wireOp",EDGE,"E13");var subQ2=makeQuery(id+"F6.imprint","INTERSECT",VERTEX,{"disambiguationData":[OD(0.0)],"derivedFrom":[subQ1,subQ0]});Q10=makeQuery(id+"F6.imprint","IMPRINT",FACE,{"disambiguationData":[TD([[makeQuery(id+"F6.imprint","IMPRINT",EDGE,{"disambiguationData":[TD([[subQ2,-1.0]])],"derivedFrom":subQ1}),-1.0]])]});}
            var Q11;
            {var subQ0=sQuery(id+"F6.wireOp",EDGE,"E31");var subQ1=sQuery(id+"F6.wireOp",EDGE,"E13");var subQ2=makeQuery(id+"F6.imprint","INTERSECT",VERTEX,{"disambiguationData":[OD(0.0)],"derivedFrom":[subQ1,subQ0]});Q11=makeQuery(id+"F6.imprint","IMPRINT",FACE,{"disambiguationData":[TD([[makeQuery(id+"F6.imprint","IMPRINT",EDGE,{"disambiguationData":[TD([[subQ2,-1.0]])],"derivedFrom":subQ1}),1.0]])]});}
            extrude(context, id + "F11", {"entities" : qUnion([Q0, Q1, Q2, Q3, Q4, Q5, Q6, Q7, Q8, Q9, Q10, Q11]), "operationType" : NewBodyOperationType.REMOVE, "depth" : 1.8 * mm, "offsetDistance" : 25 * mm});
        }
        {
            var Q0;
            Q0=qCreatedBy(makeId("Top.planeOp"),FACE);
            var sketch = newSketch(context, id + "F12", { "sketchPlane" : qUnion([Q0])});
            skCircle(sketch, "E37", {"center": v(0, 0) * mm, "radius": 17.33 * mm});
            skSolve(sketch);
        }
        {
            var Q0;
            Q0=makeQuery(id+"F12.imprint","IMPRINT",FACE,{"disambiguationData":[TD([[makeQuery(id+"F12.imprint","IMPRINT",EDGE,{"derivedFrom":sQuery(id+"F12.wireOp",EDGE,"E37")}),1.0]])]});
            extrude(context, id + "F13", {"entities" : qUnion([Q0]), "operationType" : NewBodyOperationType.REMOVE, "depth" : 1 * mm, "offsetDistance" : 25 * mm});
        }
    });
